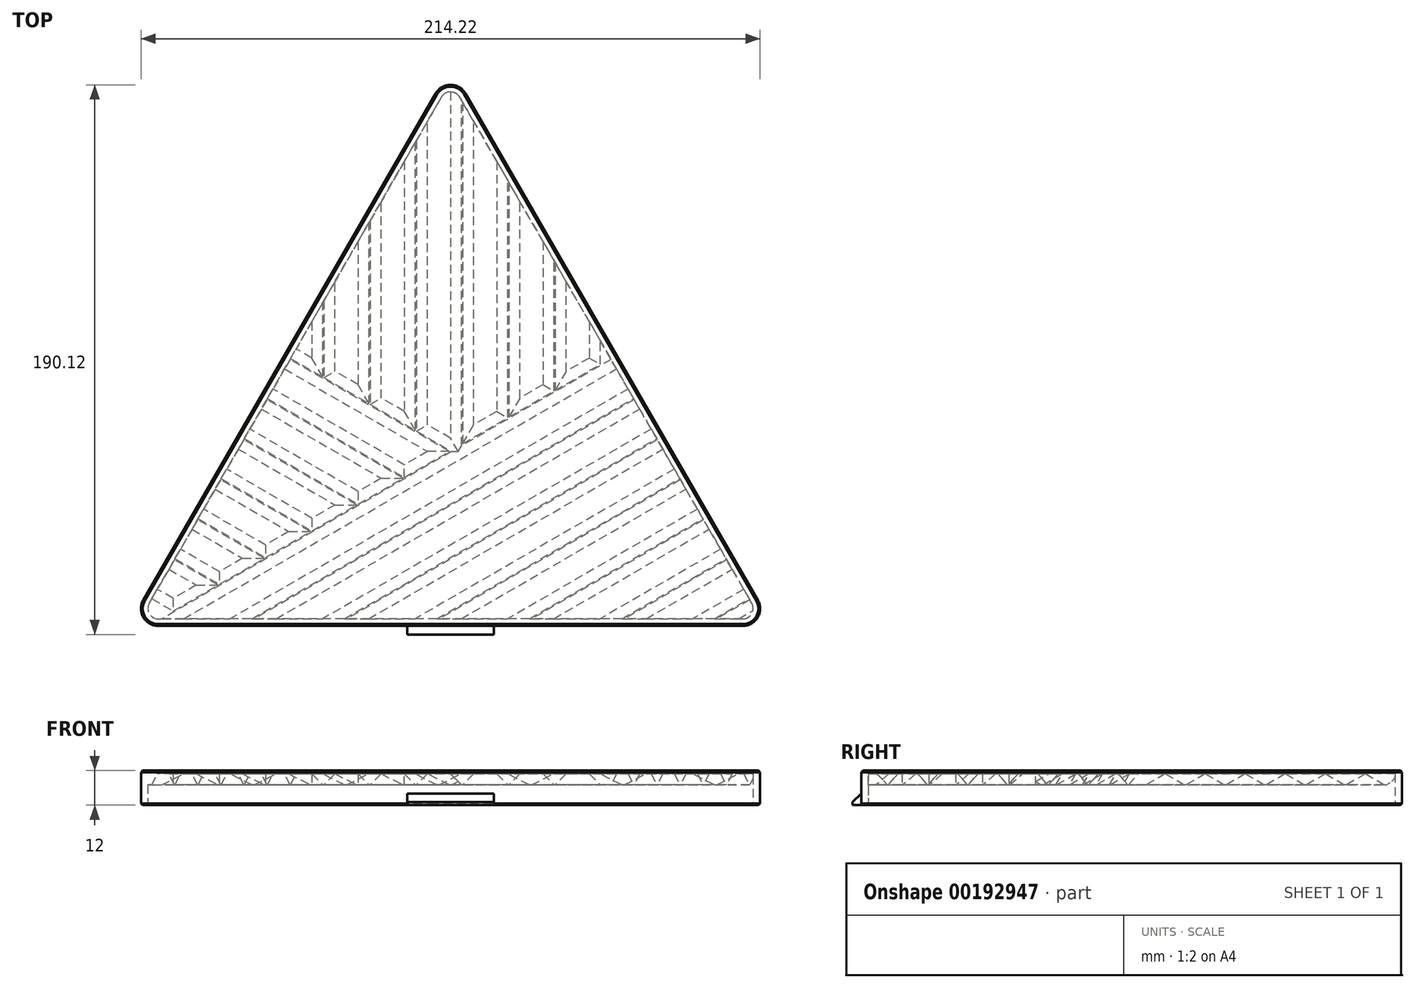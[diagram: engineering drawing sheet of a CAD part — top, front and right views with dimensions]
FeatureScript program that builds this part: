
annotation { "Feature Type Name" : "Feature", "Feature Type Description" : "" }
export const myFeature = defineFeature(function(context is Context, id is Id, definition is map)
    precondition{}
    {
        {
            var Q0;
            Q0=qCreatedBy(makeId("Top.planeOp"),FACE);
            var sketch = newSketch(context, id + "F0", { "sketchPlane" : qUnion([Q0])});
            skLineSegment(sketch, "E0", {"start": v(-5.2, -9) * mm, "end": v(-106.3, -184.12) * mm});
            skLineSegment(sketch, "E1", {"start": v(-101.1, -193.12) * mm, "end": v(101.1, -193.12) * mm});
            skLineSegment(sketch, "E2", {"start": v(106.3, -184.12) * mm, "end": v(5.2, -9) * mm});
            skPoint(sketch, "E3.visualSharp", {"position": v(-111.5, -193.12) * mm});
            skArc(sketch, "E3.filletArc", {"start": v(-106.3, -184.12) * mm, "mid": v(-106.3, -190.12) * mm, "end": v(-101.1, -193.12) * mm});
            skPoint(sketch, "E4.visualSharp", {"position": v(111.5, -193.12) * mm});
            skArc(sketch, "E4.filletArc", {"start": v(101.1, -193.12) * mm, "mid": v(106.3, -190.12) * mm, "end": v(106.3, -184.12) * mm});
            skPoint(sketch, "E5.visualSharp", {"position": v(0, 0) * mm});
            skArc(sketch, "E5.filletArc", {"start": v(5.2, -9) * mm, "mid": v(0, -6) * mm, "end": v(-5.2, -9) * mm});
            skSolve(sketch);
        }
        {
            var Q0;
            Q0=qSketchRegion(id+"F0",true);
            extrude(context, id + "F1", {"entities" : qUnion([Q0]), "depth" : 12 * mm});
        }
        {
            var Q0;
            Q0=makeQuery(id+"F1.opExtrude","CAP_FACE",FACE,{"disambiguationData":[OSD([sQuery(id+"F0.wireOp",EDGE,"E0"),sQuery(id+"F0.wireOp",EDGE,"E1"),sQuery(id+"F0.wireOp",EDGE,"E2"),sQuery(id+"F0.wireOp",EDGE,"E3.filletArc"),sQuery(id+"F0.wireOp",EDGE,"E4.filletArc"),sQuery(id+"F0.wireOp",EDGE,"E5.filletArc")])],"isStart":true});
            shell(context, id + "F2", {"entities" : qUnion([Q0]), "thickness" : 1 * mm});
        }
        {
            var Q0;
            Q0=makeQuery(id+"F1.opExtrude","CAP_FACE",FACE,{"disambiguationData":[OSD([sQuery(id+"F0.wireOp",EDGE,"E0"),sQuery(id+"F0.wireOp",EDGE,"E1"),sQuery(id+"F0.wireOp",EDGE,"E2"),sQuery(id+"F0.wireOp",EDGE,"E3.filletArc"),sQuery(id+"F0.wireOp",EDGE,"E4.filletArc"),sQuery(id+"F0.wireOp",EDGE,"E5.filletArc")])],"isStart":false});
            var sketch = newSketch(context, id + "F3", { "sketchPlane" : qUnion([Q0])});
            skArc(sketch, "E6.0.0", {"start": v(5.2, -9) * mm, "mid": v(0, -6) * mm, "end": v(-5.2, -9) * mm});
            skLineSegment(sketch, "E6.0.1", {"start": v(-5.2, -9) * mm, "end": v(-106.3, -184.12) * mm});
            skArc(sketch, "E6.0.2", {"start": v(-105.74, -183.31) * mm, "mid": v(-106.53, -189.68) * mm, "end": v(-101.1, -193.12) * mm});
            skLineSegment(sketch, "E6.0.3", {"start": v(-101.1, -193.12) * mm, "end": v(101.1, -193.12) * mm});
            skArc(sketch, "E6.0.4", {"start": v(101.1, -193.12) * mm, "mid": v(106.3, -190.12) * mm, "end": v(106.3, -184.12) * mm});
            skLineSegment(sketch, "E6.0.5", {"start": v(106.3, -184.12) * mm, "end": v(5.2, -9) * mm});
            skLineSegment(sketch, "E7", {"start": v(55.5, -96.13) * mm, "end": v(-105.8, -189.26) * mm});
            skLineSegment(sketch, "E8", {"start": v(-55.5, -96.13) * mm, "end": v(0, -128.17) * mm});
            skLineSegment(sketch, "E9", {"start": v(0, -6) * mm, "end": v(0, -128.17) * mm});
            skLineSegment(sketch, "E10.1.0.0", {"start": v(8, -6) * mm, "end": v(8, -123.55) * mm});
            skLineSegment(sketch, "E10.2.0.0", {"start": v(16, -6) * mm, "end": v(16, -118.93) * mm});
            skLineSegment(sketch, "E10.3.0.0", {"start": v(24, -6) * mm, "end": v(24, -114.32) * mm});
            skLineSegment(sketch, "E10.4.0.0", {"start": v(32, -6) * mm, "end": v(32, -109.7) * mm});
            skLineSegment(sketch, "E10.5.0.0", {"start": v(40, -6) * mm, "end": v(40, -105.08) * mm});
            skLineSegment(sketch, "E10.6.0.0", {"start": v(48, -6) * mm, "end": v(48, -100.46) * mm});
            skLineSegment(sketch, "E10.7.0.0", {"start": v(56, -6) * mm, "end": v(56, -97) * mm});
            skLineSegment(sketch, "E10.direction1", {"start": v(0, -128.17) * mm, "end": v(8, -128.17) * mm, "construction": true});
            skLineSegment(sketch, "E11.1.0.0", {"start": v(-8, -6) * mm, "end": v(-8, -123.55) * mm});
            skLineSegment(sketch, "E11.2.0.0", {"start": v(-16, -6) * mm, "end": v(-16, -118.93) * mm});
            skLineSegment(sketch, "E11.3.0.0", {"start": v(-24, -6) * mm, "end": v(-24, -114.32) * mm});
            skLineSegment(sketch, "E11.4.0.0", {"start": v(-32, -6) * mm, "end": v(-32, -109.7) * mm});
            skLineSegment(sketch, "E11.5.0.0", {"start": v(-40, -6) * mm, "end": v(-40, -105.08) * mm});
            skLineSegment(sketch, "E11.6.0.0", {"start": v(-48, -6) * mm, "end": v(-48, -100.46) * mm});
            skLineSegment(sketch, "E11.7.0.0", {"start": v(-56, -6) * mm, "end": v(-56, -97) * mm});
            skLineSegment(sketch, "E11.direction1", {"start": v(0, -128.17) * mm, "end": v(-8, -128.17) * mm, "construction": true});
            skPoint(sketch, "E12.orphan", {"position": v(-56, -128.17) * mm});
            skPoint(sketch, "E13.orphan", {"position": v(-48, -128.17) * mm});
            skPoint(sketch, "E14.orphan", {"position": v(-40, -128.17) * mm});
            skPoint(sketch, "E15.orphan", {"position": v(-32, -128.17) * mm});
            skPoint(sketch, "E16.orphan", {"position": v(-24, -128.17) * mm});
            skPoint(sketch, "E17.orphan", {"position": v(-16, -128.17) * mm});
            skPoint(sketch, "E18.orphan", {"position": v(56, -128.17) * mm});
            skPoint(sketch, "E19.orphan", {"position": v(48, -128.17) * mm});
            skPoint(sketch, "E20.orphan", {"position": v(40, -128.17) * mm});
            skPoint(sketch, "E21.orphan", {"position": v(32, -128.17) * mm});
            skPoint(sketch, "E22.orphan", {"position": v(24, -128.17) * mm});
            skPoint(sketch, "E23.orphan", {"position": v(16, -128.17) * mm});
            skLineSegment(sketch, "E24.1.0.0", {"start": v(-59.49, -103.06) * mm, "end": v(-8, -132.8) * mm});
            skLineSegment(sketch, "E24.2.0.0", {"start": v(-63.48, -110) * mm, "end": v(-16, -137.4) * mm});
            skLineSegment(sketch, "E24.3.0.0", {"start": v(-67.46, -116.93) * mm, "end": v(-24, -142.03) * mm});
            skLineSegment(sketch, "E24.4.0.0", {"start": v(-71.45, -123.87) * mm, "end": v(-32, -146.65) * mm});
            skLineSegment(sketch, "E24.5.0.0", {"start": v(-75.44, -130.8) * mm, "end": v(-40, -151.27) * mm});
            skLineSegment(sketch, "E24.6.0.0", {"start": v(-79.43, -137.74) * mm, "end": v(-48, -155.88) * mm});
            skLineSegment(sketch, "E24.7.0.0", {"start": v(-83.41, -144.68) * mm, "end": v(-56, -160.5) * mm});
            skLineSegment(sketch, "E24.8.0.0", {"start": v(-87.4, -151.61) * mm, "end": v(-64, -165.12) * mm});
            skLineSegment(sketch, "E24.9.0.0", {"start": v(-91.39, -158.55) * mm, "end": v(-72, -169.74) * mm});
            skLineSegment(sketch, "E24.10.0.0", {"start": v(-95.38, -165.48) * mm, "end": v(-80, -174.36) * mm});
            skLineSegment(sketch, "E24.11.0.0", {"start": v(-99.36, -172.42) * mm, "end": v(-88, -178.98) * mm});
            skLineSegment(sketch, "E24.12.0.0", {"start": v(-103.35, -179.35) * mm, "end": v(-96, -183.6) * mm});
            skLineSegment(sketch, "E24.13.0.0", {"start": v(-107.34, -186.29) * mm, "end": v(-104, -188.22) * mm});
            skLineSegment(sketch, "E24.direction1", {"start": v(-55.5, -96.13) * mm, "end": v(-59.49, -103.06) * mm, "construction": true});
            skLineSegment(sketch, "E25.1.0.0", {"start": v(59.5, -103.05) * mm, "end": v(-101.8, -196.18) * mm});
            skLineSegment(sketch, "E25.2.0.0", {"start": v(63.51, -109.98) * mm, "end": v(-97.8, -203.1) * mm});
            skLineSegment(sketch, "E25.3.0.0", {"start": v(67.52, -116.9) * mm, "end": v(-93.79, -210.03) * mm});
            skLineSegment(sketch, "E25.4.0.0", {"start": v(71.52, -123.83) * mm, "end": v(-89.78, -216.96) * mm});
            skLineSegment(sketch, "E25.5.0.0", {"start": v(75.53, -130.75) * mm, "end": v(-85.78, -223.88) * mm});
            skLineSegment(sketch, "E25.6.0.0", {"start": v(79.53, -137.68) * mm, "end": v(-81.77, -230.8) * mm});
            skLineSegment(sketch, "E25.7.0.0", {"start": v(83.54, -144.6) * mm, "end": v(-77.77, -237.73) * mm});
            skLineSegment(sketch, "E25.8.0.0", {"start": v(87.54, -151.53) * mm, "end": v(-73.76, -244.66) * mm});
            skLineSegment(sketch, "E25.9.0.0", {"start": v(91.55, -158.46) * mm, "end": v(-69.76, -251.58) * mm});
            skLineSegment(sketch, "E25.10.0.0", {"start": v(95.55, -165.38) * mm, "end": v(-65.75, -258.5) * mm});
            skLineSegment(sketch, "E25.11.0.0", {"start": v(99.56, -172.3) * mm, "end": v(-61.75, -265.43) * mm});
            skLineSegment(sketch, "E25.12.0.0", {"start": v(103.56, -179.23) * mm, "end": v(-57.74, -272.36) * mm});
            skLineSegment(sketch, "E25.13.0.0", {"start": v(107.57, -186.16) * mm, "end": v(-53.73, -279.28) * mm});
            skLineSegment(sketch, "E25.direction1", {"start": v(-105.8, -189.26) * mm, "end": v(-101.8, -196.18) * mm, "construction": true});
            skLineSegment(sketch, "E26.trimOffspring", {"start": v(8, -132.8) * mm, "end": v(16, -137.4) * mm});
            skLineSegment(sketch, "E27.trimOffspring", {"start": v(0, -137.4) * mm, "end": v(8, -142.03) * mm});
            skLineSegment(sketch, "E28.trimOffspring", {"start": v(-8, -142.03) * mm, "end": v(0, -146.65) * mm});
            skLineSegment(sketch, "E29.trimOffspring", {"start": v(-16, -146.65) * mm, "end": v(-8, -151.27) * mm});
            skLineSegment(sketch, "E30.trimOffspring", {"start": v(-24, -151.27) * mm, "end": v(-16, -155.88) * mm});
            skLineSegment(sketch, "E31.trimOffspring", {"start": v(-32, -155.88) * mm, "end": v(-24, -160.5) * mm});
            skLineSegment(sketch, "E32.trimOffspring", {"start": v(-40, -160.5) * mm, "end": v(-32, -165.12) * mm});
            skLineSegment(sketch, "E33.trimOffspring", {"start": v(-48, -165.12) * mm, "end": v(-40, -169.74) * mm});
            skLineSegment(sketch, "E34.trimOffspring", {"start": v(-56, -169.74) * mm, "end": v(-48, -174.36) * mm});
            skLineSegment(sketch, "E35.trimOffspring", {"start": v(-64, -174.36) * mm, "end": v(64.72, -248.68) * mm});
            skLineSegment(sketch, "E36.trimOffspring", {"start": v(-72, -178.98) * mm, "end": v(60.73, -255.61) * mm});
            skLineSegment(sketch, "E37.trimOffspring", {"start": v(-80, -183.6) * mm, "end": v(56.74, -262.55) * mm});
            skLineSegment(sketch, "E38.trimOffspring", {"start": v(-88, -188.22) * mm, "end": v(52.76, -269.48) * mm});
            skLineSegment(sketch, "E39.trimOffspring", {"start": v(-97, -192.26) * mm, "end": v(48.77, -276.42) * mm});
            skLineSegment(sketch, "E40.trimOffspring", {"start": v(24, -142.03) * mm, "end": v(100.6, -186.26) * mm});
            skLineSegment(sketch, "E41.trimOffspring", {"start": v(16, -146.65) * mm, "end": v(96.62, -193.2) * mm});
            skLineSegment(sketch, "E42.trimOffspring", {"start": v(8, -151.27) * mm, "end": v(92.63, -200.13) * mm});
            skLineSegment(sketch, "E43.trimOffspring", {"start": v(0, -155.88) * mm, "end": v(88.65, -207.06) * mm});
            skLineSegment(sketch, "E44.trimOffspring", {"start": v(-8, -160.5) * mm, "end": v(84.66, -214) * mm});
            skLineSegment(sketch, "E45.trimOffspring", {"start": v(-16, -165.12) * mm, "end": v(80.67, -220.93) * mm});
            skLineSegment(sketch, "E46.trimOffspring", {"start": v(-24, -169.74) * mm, "end": v(76.68, -227.87) * mm});
            skLineSegment(sketch, "E47.trimOffspring", {"start": v(-32, -174.36) * mm, "end": v(72.7, -234.8) * mm});
            skLineSegment(sketch, "E48.trimOffspring", {"start": v(-40, -178.98) * mm, "end": v(68.7, -241.74) * mm});
            skSolve(sketch);
        }
        {
            var Q0;
            {var subQ0=sQuery(id+"F3.wireOp",EDGE,"E11.5.0.0");var subQ1=sQuery(id+"F3.wireOp",EDGE,"E6.0.1");var subQ2=makeQuery(id+"F3.imprint","INTERSECT",VERTEX,{"derivedFrom":[subQ1,subQ0]});Q0=makeQuery(id+"F3.imprint","IMPRINT",FACE,{"disambiguationData":[TD([[makeQuery(id+"F3.imprint","IMPRINT",EDGE,{"disambiguationData":[TD([[subQ2,-1.0]])],"derivedFrom":subQ1}),1.0]])]});}
            var Q1;
            {var subQ0=sQuery(id+"F3.wireOp",EDGE,"E11.3.0.0");var subQ1=sQuery(id+"F3.wireOp",EDGE,"E6.0.1");var subQ2=makeQuery(id+"F3.imprint","INTERSECT",VERTEX,{"derivedFrom":[subQ1,subQ0]});Q1=makeQuery(id+"F3.imprint","IMPRINT",FACE,{"disambiguationData":[TD([[makeQuery(id+"F3.imprint","IMPRINT",EDGE,{"disambiguationData":[TD([[subQ2,-1.0]])],"derivedFrom":subQ1}),1.0]])]});}
            var Q2;
            {var subQ0=sQuery(id+"F3.wireOp",EDGE,"E11.1.0.0");var subQ1=sQuery(id+"F3.wireOp",EDGE,"E6.0.1");var subQ2=makeQuery(id+"F3.imprint","INTERSECT",VERTEX,{"derivedFrom":[subQ1,subQ0]});Q2=makeQuery(id+"F3.imprint","IMPRINT",FACE,{"disambiguationData":[TD([[makeQuery(id+"F3.imprint","IMPRINT",EDGE,{"disambiguationData":[TD([[subQ2,-1.0]])],"derivedFrom":subQ1}),1.0]])]});}
            var Q3;
            {var subQ0=sQuery(id+"F3.wireOp",EDGE,"E9");Q3=makeQuery(id+"F3.imprint","IMPRINT",FACE,{"disambiguationData":[TD([[makeQuery(id+"F3.imprint","IMPRINT",EDGE,{"derivedFrom":subQ0}),1.0]])]});}
            var Q4;
            {var subQ0=sQuery(id+"F3.wireOp",EDGE,"E10.3.0.0");var subQ1=sQuery(id+"F3.wireOp",EDGE,"E6.0.5");var subQ2=makeQuery(id+"F3.imprint","INTERSECT",VERTEX,{"derivedFrom":[subQ1,subQ0]});Q4=makeQuery(id+"F3.imprint","IMPRINT",FACE,{"disambiguationData":[TD([[makeQuery(id+"F3.imprint","IMPRINT",EDGE,{"disambiguationData":[TD([[subQ2,-1.0]])],"derivedFrom":subQ1}),1.0]])]});}
            var Q5;
            {var subQ0=sQuery(id+"F3.wireOp",EDGE,"E10.5.0.0");var subQ1=sQuery(id+"F3.wireOp",EDGE,"E6.0.5");var subQ2=makeQuery(id+"F3.imprint","INTERSECT",VERTEX,{"derivedFrom":[subQ1,subQ0]});Q5=makeQuery(id+"F3.imprint","IMPRINT",FACE,{"disambiguationData":[TD([[makeQuery(id+"F3.imprint","IMPRINT",EDGE,{"disambiguationData":[TD([[subQ2,-1.0]])],"derivedFrom":subQ1}),1.0]])]});}
            var Q6;
            {var subQ0=sQuery(id+"F3.wireOp",EDGE,"E7");var subQ1=sQuery(id+"F3.wireOp",EDGE,"E6.0.5");var subQ2=makeQuery(id+"F3.imprint","INTERSECT",VERTEX,{"derivedFrom":[subQ1,subQ0]});Q6=makeQuery(id+"F3.imprint","IMPRINT",FACE,{"disambiguationData":[TD([[makeQuery(id+"F3.imprint","IMPRINT",EDGE,{"disambiguationData":[TD([[subQ2,-1.0]])],"derivedFrom":subQ1}),1.0]])]});}
            var Q7;
            {var subQ0=sQuery(id+"F3.wireOp",EDGE,"E7");var subQ17=makeQuery(id+"F3.imprint","IMPRINT",VERTEX,{"disambiguationData":[OD(0.0)],"derivedFrom":subQ0});Q7=makeQuery(id+"F3.imprint","IMPRINT",FACE,{"disambiguationData":[TD([[makeQuery(id+"F3.imprint","IMPRINT",EDGE,{"disambiguationData":[TD([[subQ17,-1.0]])],"derivedFrom":subQ0}),1.0]])]});}
            var Q8;
            {var subQ5=sQuery(id+"F3.wireOp",EDGE,"E25.3.0.0");var subQ17=sQuery(id+"F3.wireOp",EDGE,"E6.0.5");var subQ20=makeQuery(id+"F3.imprint","INTERSECT",VERTEX,{"derivedFrom":[subQ17,subQ5]});Q8=makeQuery(id+"F3.imprint","IMPRINT",FACE,{"disambiguationData":[TD([[makeQuery(id+"F3.imprint","IMPRINT",EDGE,{"disambiguationData":[TD([[subQ20,-1.0]])],"derivedFrom":subQ17}),1.0]])]});}
            var Q9;
            {var subQ0=sQuery(id+"F3.wireOp",EDGE,"E35.trimOffspring");var subQ1=sQuery(id+"F3.wireOp",EDGE,"E25.2.0.0");var subQ2=makeQuery(id+"F3.imprint","INTERSECT",VERTEX,{"derivedFrom":[subQ1,subQ0]});Q9=makeQuery(id+"F3.imprint","IMPRINT",FACE,{"disambiguationData":[TD([[makeQuery(id+"F3.imprint","IMPRINT",EDGE,{"disambiguationData":[TD([[subQ2,-1.0]])],"derivedFrom":subQ1}),1.0]])]});}
            var Q10;
            {var subQ0=sQuery(id+"F3.wireOp",EDGE,"E25.2.0.0");var subQ1=sQuery(id+"F3.wireOp",EDGE,"E6.0.3");var subQ2=makeQuery(id+"F3.imprint","INTERSECT",VERTEX,{"derivedFrom":[subQ1,subQ0]});Q10=makeQuery(id+"F3.imprint","IMPRINT",FACE,{"disambiguationData":[TD([[makeQuery(id+"F3.imprint","IMPRINT",EDGE,{"disambiguationData":[TD([[subQ2,-1.0]])],"derivedFrom":subQ1}),1.0]])]});}
            var Q11;
            {var subQ0=sQuery(id+"F3.wireOp",EDGE,"E25.5.0.0");var subQ1=sQuery(id+"F3.wireOp",EDGE,"E6.0.5");var subQ2=makeQuery(id+"F3.imprint","INTERSECT",VERTEX,{"derivedFrom":[subQ1,subQ0]});Q11=makeQuery(id+"F3.imprint","IMPRINT",FACE,{"disambiguationData":[TD([[makeQuery(id+"F3.imprint","IMPRINT",EDGE,{"disambiguationData":[TD([[subQ2,-1.0]])],"derivedFrom":subQ1}),1.0]])]});}
            var Q12;
            {var subQ0=sQuery(id+"F3.wireOp",EDGE,"E40.trimOffspring");var subQ1=sQuery(id+"F3.wireOp",EDGE,"E25.4.0.0");var subQ2=makeQuery(id+"F3.imprint","INTERSECT",VERTEX,{"derivedFrom":[subQ1,subQ0]});Q12=makeQuery(id+"F3.imprint","IMPRINT",FACE,{"disambiguationData":[TD([[makeQuery(id+"F3.imprint","IMPRINT",EDGE,{"disambiguationData":[TD([[subQ2,-1.0]])],"derivedFrom":subQ1}),1.0]])]});}
            var Q13;
            {var subQ0=sQuery(id+"F3.wireOp",EDGE,"E41.trimOffspring");var subQ1=sQuery(id+"F3.wireOp",EDGE,"E25.4.0.0");var subQ2=makeQuery(id+"F3.imprint","INTERSECT",VERTEX,{"derivedFrom":[subQ1,subQ0]});Q13=makeQuery(id+"F3.imprint","IMPRINT",FACE,{"disambiguationData":[TD([[makeQuery(id+"F3.imprint","IMPRINT",EDGE,{"disambiguationData":[TD([[subQ2,-1.0]])],"derivedFrom":subQ1}),1.0]])]});}
            var Q14;
            {var subQ0=sQuery(id+"F3.wireOp",EDGE,"E42.trimOffspring");var subQ1=sQuery(id+"F3.wireOp",EDGE,"E25.4.0.0");var subQ2=makeQuery(id+"F3.imprint","INTERSECT",VERTEX,{"derivedFrom":[subQ1,subQ0]});Q14=makeQuery(id+"F3.imprint","IMPRINT",FACE,{"disambiguationData":[TD([[makeQuery(id+"F3.imprint","IMPRINT",EDGE,{"disambiguationData":[TD([[subQ2,-1.0]])],"derivedFrom":subQ1}),1.0]])]});}
            var Q15;
            {var subQ0=sQuery(id+"F3.wireOp",EDGE,"E43.trimOffspring");var subQ1=sQuery(id+"F3.wireOp",EDGE,"E25.4.0.0");var subQ2=makeQuery(id+"F3.imprint","INTERSECT",VERTEX,{"derivedFrom":[subQ1,subQ0]});Q15=makeQuery(id+"F3.imprint","IMPRINT",FACE,{"disambiguationData":[TD([[makeQuery(id+"F3.imprint","IMPRINT",EDGE,{"disambiguationData":[TD([[subQ2,-1.0]])],"derivedFrom":subQ1}),1.0]])]});}
            var Q16;
            {var subQ0=sQuery(id+"F3.wireOp",EDGE,"E44.trimOffspring");var subQ1=sQuery(id+"F3.wireOp",EDGE,"E25.4.0.0");var subQ2=makeQuery(id+"F3.imprint","INTERSECT",VERTEX,{"derivedFrom":[subQ1,subQ0]});Q16=makeQuery(id+"F3.imprint","IMPRINT",FACE,{"disambiguationData":[TD([[makeQuery(id+"F3.imprint","IMPRINT",EDGE,{"disambiguationData":[TD([[subQ2,-1.0]])],"derivedFrom":subQ1}),1.0]])]});}
            var Q17;
            {var subQ0=sQuery(id+"F3.wireOp",EDGE,"E45.trimOffspring");var subQ1=sQuery(id+"F3.wireOp",EDGE,"E25.4.0.0");var subQ2=makeQuery(id+"F3.imprint","INTERSECT",VERTEX,{"derivedFrom":[subQ1,subQ0]});Q17=makeQuery(id+"F3.imprint","IMPRINT",FACE,{"disambiguationData":[TD([[makeQuery(id+"F3.imprint","IMPRINT",EDGE,{"disambiguationData":[TD([[subQ2,-1.0]])],"derivedFrom":subQ1}),1.0]])]});}
            var Q18;
            {var subQ0=sQuery(id+"F3.wireOp",EDGE,"E46.trimOffspring");var subQ1=sQuery(id+"F3.wireOp",EDGE,"E25.4.0.0");var subQ2=makeQuery(id+"F3.imprint","INTERSECT",VERTEX,{"derivedFrom":[subQ1,subQ0]});Q18=makeQuery(id+"F3.imprint","IMPRINT",FACE,{"disambiguationData":[TD([[makeQuery(id+"F3.imprint","IMPRINT",EDGE,{"disambiguationData":[TD([[subQ2,-1.0]])],"derivedFrom":subQ1}),1.0]])]});}
            var Q19;
            {var subQ0=sQuery(id+"F3.wireOp",EDGE,"E47.trimOffspring");var subQ1=sQuery(id+"F3.wireOp",EDGE,"E25.4.0.0");var subQ2=makeQuery(id+"F3.imprint","INTERSECT",VERTEX,{"derivedFrom":[subQ1,subQ0]});Q19=makeQuery(id+"F3.imprint","IMPRINT",FACE,{"disambiguationData":[TD([[makeQuery(id+"F3.imprint","IMPRINT",EDGE,{"disambiguationData":[TD([[subQ2,-1.0]])],"derivedFrom":subQ1}),1.0]])]});}
            var Q20;
            {var subQ0=sQuery(id+"F3.wireOp",EDGE,"E25.4.0.0");var subQ1=sQuery(id+"F3.wireOp",EDGE,"E6.0.3");var subQ2=makeQuery(id+"F3.imprint","INTERSECT",VERTEX,{"derivedFrom":[subQ1,subQ0]});Q20=makeQuery(id+"F3.imprint","IMPRINT",FACE,{"disambiguationData":[TD([[makeQuery(id+"F3.imprint","IMPRINT",EDGE,{"disambiguationData":[TD([[subQ2,-1.0]])],"derivedFrom":subQ1}),1.0]])]});}
            var Q21;
            {var subQ0=sQuery(id+"F3.wireOp",EDGE,"E25.6.0.0");var subQ1=sQuery(id+"F3.wireOp",EDGE,"E6.0.3");var subQ2=makeQuery(id+"F3.imprint","INTERSECT",VERTEX,{"derivedFrom":[subQ1,subQ0]});Q21=makeQuery(id+"F3.imprint","IMPRINT",FACE,{"disambiguationData":[TD([[makeQuery(id+"F3.imprint","IMPRINT",EDGE,{"disambiguationData":[TD([[subQ2,-1.0]])],"derivedFrom":subQ1}),1.0]])]});}
            var Q22;
            {var subQ0=sQuery(id+"F3.wireOp",EDGE,"E45.trimOffspring");var subQ1=sQuery(id+"F3.wireOp",EDGE,"E25.6.0.0");var subQ2=makeQuery(id+"F3.imprint","INTERSECT",VERTEX,{"derivedFrom":[subQ1,subQ0]});Q22=makeQuery(id+"F3.imprint","IMPRINT",FACE,{"disambiguationData":[TD([[makeQuery(id+"F3.imprint","IMPRINT",EDGE,{"disambiguationData":[TD([[subQ2,-1.0]])],"derivedFrom":subQ1}),1.0]])]});}
            var Q23;
            {var subQ0=sQuery(id+"F3.wireOp",EDGE,"E44.trimOffspring");var subQ1=sQuery(id+"F3.wireOp",EDGE,"E25.6.0.0");var subQ2=makeQuery(id+"F3.imprint","INTERSECT",VERTEX,{"derivedFrom":[subQ1,subQ0]});Q23=makeQuery(id+"F3.imprint","IMPRINT",FACE,{"disambiguationData":[TD([[makeQuery(id+"F3.imprint","IMPRINT",EDGE,{"disambiguationData":[TD([[subQ2,-1.0]])],"derivedFrom":subQ1}),1.0]])]});}
            var Q24;
            {var subQ0=sQuery(id+"F3.wireOp",EDGE,"E43.trimOffspring");var subQ1=sQuery(id+"F3.wireOp",EDGE,"E25.6.0.0");var subQ2=makeQuery(id+"F3.imprint","INTERSECT",VERTEX,{"derivedFrom":[subQ1,subQ0]});Q24=makeQuery(id+"F3.imprint","IMPRINT",FACE,{"disambiguationData":[TD([[makeQuery(id+"F3.imprint","IMPRINT",EDGE,{"disambiguationData":[TD([[subQ2,-1.0]])],"derivedFrom":subQ1}),1.0]])]});}
            var Q25;
            {var subQ0=sQuery(id+"F3.wireOp",EDGE,"E42.trimOffspring");var subQ1=sQuery(id+"F3.wireOp",EDGE,"E25.6.0.0");var subQ2=makeQuery(id+"F3.imprint","INTERSECT",VERTEX,{"derivedFrom":[subQ1,subQ0]});Q25=makeQuery(id+"F3.imprint","IMPRINT",FACE,{"disambiguationData":[TD([[makeQuery(id+"F3.imprint","IMPRINT",EDGE,{"disambiguationData":[TD([[subQ2,-1.0]])],"derivedFrom":subQ1}),1.0]])]});}
            var Q26;
            {var subQ0=sQuery(id+"F3.wireOp",EDGE,"E41.trimOffspring");var subQ1=sQuery(id+"F3.wireOp",EDGE,"E25.6.0.0");var subQ2=makeQuery(id+"F3.imprint","INTERSECT",VERTEX,{"derivedFrom":[subQ1,subQ0]});Q26=makeQuery(id+"F3.imprint","IMPRINT",FACE,{"disambiguationData":[TD([[makeQuery(id+"F3.imprint","IMPRINT",EDGE,{"disambiguationData":[TD([[subQ2,-1.0]])],"derivedFrom":subQ1}),1.0]])]});}
            var Q27;
            {var subQ0=sQuery(id+"F3.wireOp",EDGE,"E40.trimOffspring");var subQ1=sQuery(id+"F3.wireOp",EDGE,"E25.6.0.0");var subQ2=makeQuery(id+"F3.imprint","INTERSECT",VERTEX,{"derivedFrom":[subQ1,subQ0]});Q27=makeQuery(id+"F3.imprint","IMPRINT",FACE,{"disambiguationData":[TD([[makeQuery(id+"F3.imprint","IMPRINT",EDGE,{"disambiguationData":[TD([[subQ2,-1.0]])],"derivedFrom":subQ1}),1.0]])]});}
            var Q28;
            {var subQ0=sQuery(id+"F3.wireOp",EDGE,"E25.7.0.0");var subQ1=sQuery(id+"F3.wireOp",EDGE,"E6.0.5");var subQ2=makeQuery(id+"F3.imprint","INTERSECT",VERTEX,{"derivedFrom":[subQ1,subQ0]});Q28=makeQuery(id+"F3.imprint","IMPRINT",FACE,{"disambiguationData":[TD([[makeQuery(id+"F3.imprint","IMPRINT",EDGE,{"disambiguationData":[TD([[subQ2,-1.0]])],"derivedFrom":subQ1}),1.0]])]});}
            var Q29;
            {var subQ0=sQuery(id+"F3.wireOp",EDGE,"E25.9.0.0");var subQ1=sQuery(id+"F3.wireOp",EDGE,"E6.0.5");var subQ2=makeQuery(id+"F3.imprint","INTERSECT",VERTEX,{"derivedFrom":[subQ1,subQ0]});Q29=makeQuery(id+"F3.imprint","IMPRINT",FACE,{"disambiguationData":[TD([[makeQuery(id+"F3.imprint","IMPRINT",EDGE,{"disambiguationData":[TD([[subQ2,-1.0]])],"derivedFrom":subQ1}),1.0]])]});}
            var Q30;
            {var subQ0=sQuery(id+"F3.wireOp",EDGE,"E40.trimOffspring");var subQ1=sQuery(id+"F3.wireOp",EDGE,"E25.8.0.0");var subQ2=makeQuery(id+"F3.imprint","INTERSECT",VERTEX,{"derivedFrom":[subQ1,subQ0]});Q30=makeQuery(id+"F3.imprint","IMPRINT",FACE,{"disambiguationData":[TD([[makeQuery(id+"F3.imprint","IMPRINT",EDGE,{"disambiguationData":[TD([[subQ2,-1.0]])],"derivedFrom":subQ1}),1.0]])]});}
            var Q31;
            {var subQ0=sQuery(id+"F3.wireOp",EDGE,"E41.trimOffspring");var subQ1=sQuery(id+"F3.wireOp",EDGE,"E25.8.0.0");var subQ2=makeQuery(id+"F3.imprint","INTERSECT",VERTEX,{"derivedFrom":[subQ1,subQ0]});Q31=makeQuery(id+"F3.imprint","IMPRINT",FACE,{"disambiguationData":[TD([[makeQuery(id+"F3.imprint","IMPRINT",EDGE,{"disambiguationData":[TD([[subQ2,-1.0]])],"derivedFrom":subQ1}),1.0]])]});}
            var Q32;
            {var subQ0=sQuery(id+"F3.wireOp",EDGE,"E43.trimOffspring");var subQ1=sQuery(id+"F3.wireOp",EDGE,"E25.8.0.0");var subQ2=makeQuery(id+"F3.imprint","INTERSECT",VERTEX,{"derivedFrom":[subQ1,subQ0]});Q32=makeQuery(id+"F3.imprint","IMPRINT",FACE,{"disambiguationData":[TD([[makeQuery(id+"F3.imprint","IMPRINT",EDGE,{"disambiguationData":[TD([[subQ2,-1.0]])],"derivedFrom":subQ1}),1.0]])]});}
            var Q33;
            {var subQ0=sQuery(id+"F3.wireOp",EDGE,"E25.8.0.0");var subQ1=sQuery(id+"F3.wireOp",EDGE,"E6.0.3");var subQ2=makeQuery(id+"F3.imprint","INTERSECT",VERTEX,{"derivedFrom":[subQ1,subQ0]});Q33=makeQuery(id+"F3.imprint","IMPRINT",FACE,{"disambiguationData":[TD([[makeQuery(id+"F3.imprint","IMPRINT",EDGE,{"disambiguationData":[TD([[subQ2,-1.0]])],"derivedFrom":subQ1}),1.0]])]});}
            var Q34;
            {var subQ0=sQuery(id+"F3.wireOp",EDGE,"E42.trimOffspring");var subQ1=sQuery(id+"F3.wireOp",EDGE,"E25.8.0.0");var subQ2=makeQuery(id+"F3.imprint","INTERSECT",VERTEX,{"derivedFrom":[subQ1,subQ0]});Q34=makeQuery(id+"F3.imprint","IMPRINT",FACE,{"disambiguationData":[TD([[makeQuery(id+"F3.imprint","IMPRINT",EDGE,{"disambiguationData":[TD([[subQ2,-1.0]])],"derivedFrom":subQ1}),1.0]])]});}
            var Q35;
            {var subQ0=sQuery(id+"F3.wireOp",EDGE,"E25.10.0.0");var subQ1=sQuery(id+"F3.wireOp",EDGE,"E6.0.3");var subQ2=makeQuery(id+"F3.imprint","INTERSECT",VERTEX,{"derivedFrom":[subQ1,subQ0]});Q35=makeQuery(id+"F3.imprint","IMPRINT",FACE,{"disambiguationData":[TD([[makeQuery(id+"F3.imprint","IMPRINT",EDGE,{"disambiguationData":[TD([[subQ2,-1.0]])],"derivedFrom":subQ1}),1.0]])]});}
            var Q36;
            {var subQ0=sQuery(id+"F3.wireOp",EDGE,"E41.trimOffspring");var subQ1=sQuery(id+"F3.wireOp",EDGE,"E25.10.0.0");var subQ2=makeQuery(id+"F3.imprint","INTERSECT",VERTEX,{"derivedFrom":[subQ1,subQ0]});Q36=makeQuery(id+"F3.imprint","IMPRINT",FACE,{"disambiguationData":[TD([[makeQuery(id+"F3.imprint","IMPRINT",EDGE,{"disambiguationData":[TD([[subQ2,-1.0]])],"derivedFrom":subQ1}),1.0]])]});}
            var Q37;
            {var subQ0=sQuery(id+"F3.wireOp",EDGE,"E40.trimOffspring");var subQ1=sQuery(id+"F3.wireOp",EDGE,"E25.10.0.0");var subQ2=makeQuery(id+"F3.imprint","INTERSECT",VERTEX,{"derivedFrom":[subQ1,subQ0]});Q37=makeQuery(id+"F3.imprint","IMPRINT",FACE,{"disambiguationData":[TD([[makeQuery(id+"F3.imprint","IMPRINT",EDGE,{"disambiguationData":[TD([[subQ2,-1.0]])],"derivedFrom":subQ1}),1.0]])]});}
            var Q38;
            {var subQ0=sQuery(id+"F3.wireOp",EDGE,"E25.11.0.0");var subQ1=sQuery(id+"F3.wireOp",EDGE,"E6.0.5");var subQ2=makeQuery(id+"F3.imprint","INTERSECT",VERTEX,{"derivedFrom":[subQ1,subQ0]});Q38=makeQuery(id+"F3.imprint","IMPRINT",FACE,{"disambiguationData":[TD([[makeQuery(id+"F3.imprint","IMPRINT",EDGE,{"disambiguationData":[TD([[subQ2,-1.0]])],"derivedFrom":subQ1}),1.0]])]});}
            var Q39;
            {var subQ0=sQuery(id+"F3.wireOp",EDGE,"E25.12.0.0");var subQ1=sQuery(id+"F3.wireOp",EDGE,"E6.0.3");var subQ2=makeQuery(id+"F3.imprint","INTERSECT",VERTEX,{"derivedFrom":[subQ1,subQ0]});Q39=makeQuery(id+"F3.imprint","IMPRINT",FACE,{"disambiguationData":[TD([[makeQuery(id+"F3.imprint","IMPRINT",EDGE,{"disambiguationData":[TD([[subQ2,-1.0]])],"derivedFrom":subQ1}),1.0]])]});}
            var Q40;
            {var subQ0=sQuery(id+"F3.wireOp",EDGE,"E42.trimOffspring");var subQ1=sQuery(id+"F3.wireOp",EDGE,"E25.10.0.0");var subQ2=makeQuery(id+"F3.imprint","INTERSECT",VERTEX,{"derivedFrom":[subQ1,subQ0]});Q40=makeQuery(id+"F3.imprint","IMPRINT",FACE,{"disambiguationData":[TD([[makeQuery(id+"F3.imprint","IMPRINT",EDGE,{"disambiguationData":[TD([[subQ2,-1.0]])],"derivedFrom":subQ1}),1.0]])]});}
            var Q41;
            {var subQ5=sQuery(id+"F3.wireOp",EDGE,"E6.0.3");var subQ7=sQuery(id+"F3.wireOp",EDGE,"E44.trimOffspring");var subQ9=makeQuery(id+"F3.imprint","INTERSECT",VERTEX,{"derivedFrom":[subQ5,subQ7]});Q41=makeQuery(id+"F3.imprint","IMPRINT",FACE,{"disambiguationData":[TD([[makeQuery(id+"F3.imprint","IMPRINT",EDGE,{"disambiguationData":[TD([[subQ9,-1.0]])],"derivedFrom":subQ5}),1.0]])]});}
            var Q42;
            {var subQ1=sQuery(id+"F3.wireOp",EDGE,"E6.0.3");var subQ7=sQuery(id+"F3.wireOp",EDGE,"E46.trimOffspring");var subQ9=makeQuery(id+"F3.imprint","INTERSECT",VERTEX,{"derivedFrom":[subQ1,subQ7]});Q42=makeQuery(id+"F3.imprint","IMPRINT",FACE,{"disambiguationData":[TD([[makeQuery(id+"F3.imprint","IMPRINT",EDGE,{"disambiguationData":[TD([[subQ9,-1.0]])],"derivedFrom":subQ1}),1.0]])]});}
            var Q43;
            {var subQ0=sQuery(id+"F3.wireOp",EDGE,"E44.trimOffspring");var subQ1=sQuery(id+"F3.wireOp",EDGE,"E25.8.0.0");var subQ2=makeQuery(id+"F3.imprint","INTERSECT",VERTEX,{"derivedFrom":[subQ1,subQ0]});Q43=makeQuery(id+"F3.imprint","IMPRINT",FACE,{"disambiguationData":[TD([[makeQuery(id+"F3.imprint","IMPRINT",EDGE,{"disambiguationData":[TD([[subQ2,-1.0]])],"derivedFrom":subQ1}),1.0]])]});}
            var Q44;
            {var subQ0=sQuery(id+"F3.wireOp",EDGE,"E46.trimOffspring");var subQ1=sQuery(id+"F3.wireOp",EDGE,"E25.6.0.0");var subQ2=makeQuery(id+"F3.imprint","INTERSECT",VERTEX,{"derivedFrom":[subQ1,subQ0]});Q44=makeQuery(id+"F3.imprint","IMPRINT",FACE,{"disambiguationData":[TD([[makeQuery(id+"F3.imprint","IMPRINT",EDGE,{"disambiguationData":[TD([[subQ2,-1.0]])],"derivedFrom":subQ1}),1.0]])]});}
            var Q45;
            {var subQ5=sQuery(id+"F3.wireOp",EDGE,"E6.0.3");var subQ7=sQuery(id+"F3.wireOp",EDGE,"E48.trimOffspring");var subQ9=makeQuery(id+"F3.imprint","INTERSECT",VERTEX,{"derivedFrom":[subQ5,subQ7]});Q45=makeQuery(id+"F3.imprint","IMPRINT",FACE,{"disambiguationData":[TD([[makeQuery(id+"F3.imprint","IMPRINT",EDGE,{"disambiguationData":[TD([[subQ9,-1.0]])],"derivedFrom":subQ5}),1.0]])]});}
            var Q46;
            {var subQ0=sQuery(id+"F3.wireOp",EDGE,"E48.trimOffspring");var subQ1=sQuery(id+"F3.wireOp",EDGE,"E25.4.0.0");var subQ2=makeQuery(id+"F3.imprint","INTERSECT",VERTEX,{"derivedFrom":[subQ1,subQ0]});Q46=makeQuery(id+"F3.imprint","IMPRINT",FACE,{"disambiguationData":[TD([[makeQuery(id+"F3.imprint","IMPRINT",EDGE,{"disambiguationData":[TD([[subQ2,-1.0]])],"derivedFrom":subQ1}),1.0]])]});}
            var Q47;
            {var subQ5=sQuery(id+"F3.wireOp",EDGE,"E6.0.3");var subQ7=sQuery(id+"F3.wireOp",EDGE,"E36.trimOffspring");var subQ9=makeQuery(id+"F3.imprint","INTERSECT",VERTEX,{"derivedFrom":[subQ5,subQ7]});Q47=makeQuery(id+"F3.imprint","IMPRINT",FACE,{"disambiguationData":[TD([[makeQuery(id+"F3.imprint","IMPRINT",EDGE,{"disambiguationData":[TD([[subQ9,-1.0]])],"derivedFrom":subQ5}),1.0]])]});}
            var Q48;
            {var subQ0=sQuery(id+"F3.wireOp",EDGE,"E36.trimOffspring");var subQ1=sQuery(id+"F3.wireOp",EDGE,"E25.2.0.0");var subQ2=makeQuery(id+"F3.imprint","INTERSECT",VERTEX,{"derivedFrom":[subQ1,subQ0]});Q48=makeQuery(id+"F3.imprint","IMPRINT",FACE,{"disambiguationData":[TD([[makeQuery(id+"F3.imprint","IMPRINT",EDGE,{"disambiguationData":[TD([[subQ2,-1.0]])],"derivedFrom":subQ1}),1.0]])]});}
            var Q49;
            {var subQ1=sQuery(id+"F3.wireOp",EDGE,"E6.0.3");var subQ7=sQuery(id+"F3.wireOp",EDGE,"E38.trimOffspring");var subQ9=makeQuery(id+"F3.imprint","INTERSECT",VERTEX,{"derivedFrom":[subQ1,subQ7]});Q49=makeQuery(id+"F3.imprint","IMPRINT",FACE,{"disambiguationData":[TD([[makeQuery(id+"F3.imprint","IMPRINT",EDGE,{"disambiguationData":[TD([[subQ9,-1.0]])],"derivedFrom":subQ1}),1.0]])]});}
            var Q50;
            {var subQ0=sQuery(id+"F3.wireOp",EDGE,"E25.13.0.0");var subQ1=sQuery(id+"F3.wireOp",EDGE,"E6.0.3");var subQ2=makeQuery(id+"F3.imprint","INTERSECT",VERTEX,{"derivedFrom":[subQ1,subQ0]});Q50=makeQuery(id+"F3.imprint","IMPRINT",FACE,{"disambiguationData":[TD([[makeQuery(id+"F3.imprint","IMPRINT",EDGE,{"disambiguationData":[TD([[subQ2,1.0]])],"derivedFrom":subQ1}),1.0]])]});}
            var Q51;
            {var subQ4=sQuery(id+"F3.wireOp",EDGE,"E6.0.5");var subQ6=sQuery(id+"F3.wireOp",EDGE,"E6.0.4");var subQ7=makeQuery(id+"F3.imprint","INTERSECT",VERTEX,{"derivedFrom":[subQ6,subQ4]});Q51=makeQuery(id+"F3.imprint","IMPRINT",FACE,{"disambiguationData":[TD([[makeQuery(id+"F3.imprint","IMPRINT",EDGE,{"disambiguationData":[TD([[subQ7,1.0]])],"derivedFrom":subQ6}),1.0]])]});}
            extrude(context, id + "F4", {"entities" : qUnion([Q0, Q1, Q2, Q3, Q4, Q5, Q6, Q7, Q8, Q9, Q10, Q11, Q12, Q13, Q14, Q15, Q16, Q17, Q18, Q19, Q20, Q21, Q22, Q23, Q24, Q25, Q26, Q27, Q28, Q29, Q30, Q31, Q32, Q33, Q34, Q35, Q36, Q37, Q38, Q39, Q40, Q41, Q42, Q43, Q44, Q45, Q46, Q47, Q48, Q49, Q50, Q51]), "operationType" : NewBodyOperationType.ADD, "oppositeDirection" : true, "depth" : 5 * mm});
        }
        {
            var Q0;
            {var subQ4=sQuery(id+"F0.wireOp",EDGE,"E0");var subQ5=sQuery(id+"F0.wireOp",EDGE,"E3.filletArc");var subQ23=sQuery(id+"F0.wireOp",EDGE,"E5.filletArc");Q0=makeQuery(id+"F4.boolean.opBoolean","SPLIT",FACE,{"disambiguationData":[TD([makeQuery(id+"F2.opShell","OFFSET_FACE",FACE,{"disambiguationData":[OSD([subQ4])]})])],"derivedFrom":makeQuery(id+"F2.opShell","OFFSET_FACE",FACE,{"disambiguationData":[OSD([subQ4,sQuery(id+"F0.wireOp",EDGE,"E1"),sQuery(id+"F0.wireOp",EDGE,"E2"),subQ5,sQuery(id+"F0.wireOp",EDGE,"E4.filletArc"),subQ23])]})});}
            var sketch = newSketch(context, id + "F5", { "sketchPlane" : qUnion([Q0])});
            skLineSegment(sketch, "E49", {"start": v(0, 128.17) * mm, "end": v(-54.63, 96.63) * mm});
            skLineSegment(sketch, "E50.1.0.0", {"start": v(-4.04, 135.08) * mm, "end": v(-58.67, 103.53) * mm});
            skLineSegment(sketch, "E50.2.0.0", {"start": v(-8.08, 141.98) * mm, "end": v(-62.71, 110.44) * mm});
            skLineSegment(sketch, "E50.3.0.0", {"start": v(-12.12, 148.89) * mm, "end": v(-66.75, 117.35) * mm});
            skLineSegment(sketch, "E50.4.0.0", {"start": v(-16.16, 155.8) * mm, "end": v(-70.8, 124.25) * mm});
            skLineSegment(sketch, "E50.5.0.0", {"start": v(-20.2, 162.7) * mm, "end": v(-74.83, 131.16) * mm});
            skLineSegment(sketch, "E50.6.0.0", {"start": v(-24.23, 169.6) * mm, "end": v(-78.87, 138.06) * mm});
            skLineSegment(sketch, "E50.7.0.0", {"start": v(-28.27, 176.5) * mm, "end": v(-82.9, 144.97) * mm});
            skLineSegment(sketch, "E50.8.0.0", {"start": v(-32.31, 183.42) * mm, "end": v(-86.95, 151.87) * mm});
            skLineSegment(sketch, "E50.9.0.0", {"start": v(-36.35, 190.32) * mm, "end": v(-90.99, 158.78) * mm});
            skLineSegment(sketch, "E50.10.0.0", {"start": v(-40.4, 197.23) * mm, "end": v(-95.03, 165.68) * mm});
            skLineSegment(sketch, "E50.11.0.0", {"start": v(-44.43, 204.13) * mm, "end": v(-99.06, 172.59) * mm});
            skLineSegment(sketch, "E50.12.0.0", {"start": v(-48.47, 211.04) * mm, "end": v(-103.1, 179.5) * mm});
            skLineSegment(sketch, "E50.13.0.0", {"start": v(-52.5, 217.94) * mm, "end": v(-107.14, 186.4) * mm});
            skLineSegment(sketch, "E50.direction1", {"start": v(-54.63, 96.63) * mm, "end": v(-58.67, 103.53) * mm, "construction": true});
            skSolve(sketch);
        }
        {
            var Q0;
            {var subQ0=sQuery(id+"F5.wireOp",EDGE,"E49");var subQ1=sQuery(id+"F0.wireOp",EDGE,"E3.filletArc");var subQ2=sQuery(id+"F0.wireOp",EDGE,"E0");var subQ3=makeQuery(id+"F2.opShell","OFFSET_FACE",FACE,{"disambiguationData":[OSD([subQ2,sQuery(id+"F0.wireOp",EDGE,"E1"),sQuery(id+"F0.wireOp",EDGE,"E2"),subQ1,sQuery(id+"F0.wireOp",EDGE,"E4.filletArc"),sQuery(id+"F0.wireOp",EDGE,"E5.filletArc")])]});var subQ6=makeQuery(id+"F4.opExtrude","SWEPT_FACE",FACE,{"disambiguationData":[OSD([sQuery(id+"F3.wireOp",EDGE,"E11.6.0.0")])]});var subQ7=makeQuery(id+"F5.imprint","INTERSECT",VERTEX,{"derivedFrom":[makeQuery(id+"F4.boolean.opBoolean","INTERSECT",EDGE,{"derivedFrom":[subQ3,subQ6]}),subQ0]});var subQ29=makeQuery(id+"F5.imprint","INTERSECT",VERTEX,{"derivedFrom":[makeQuery(id+"F4.boolean.opBoolean","INTERSECT",EDGE,{"derivedFrom":[subQ3,makeQuery(id+"F4.opExtrude","SWEPT_FACE",FACE,{"disambiguationData":[OSD([sQuery(id+"F3.wireOp",EDGE,"E11.5.0.0")])]})]}),subQ0]});Q0=makeQuery(id+"F5.imprint","IMPRINT",FACE,{"disambiguationData":[TD([[makeQuery(id+"F5.imprint","IMPRINT",EDGE,{"disambiguationData":[TD([[subQ29,1.0],[subQ7,-1.0]])],"derivedFrom":subQ0}),1.0]])]});}
            var Q1;
            {var subQ0=sQuery(id+"F5.wireOp",EDGE,"E50.2.0.0");var subQ15=sQuery(id+"F0.wireOp",EDGE,"E3.filletArc");var subQ16=sQuery(id+"F0.wireOp",EDGE,"E0");var subQ20=makeQuery(id+"F4.boolean.opBoolean","SPLIT",EDGE,{"disambiguationData":[TD([makeQuery(id+"F2.opShell","OFFSET_FACE",FACE,{"disambiguationData":[OSD([subQ15])]})])],"derivedFrom":makeQuery(id+"F2.opShell","OFFSET_EDGE",EDGE,{"disambiguationData":[OSD([subQ16]),TDD([makeQuery(id+"F1.opExtrude","CAP_EDGE",EDGE,{"disambiguationData":[OSD([subQ16])],"isStart":false})])]})});var subQ21=makeQuery(id+"F5.imprint","INTERSECT",VERTEX,{"derivedFrom":[subQ20,subQ0]});Q1=makeQuery(id+"F5.imprint","IMPRINT",FACE,{"disambiguationData":[TD([[makeQuery(id+"F5.imprint","IMPRINT",EDGE,{"disambiguationData":[TD([[subQ21,-1.0]])],"derivedFrom":subQ20}),-1.0]])]});}
            var Q2;
            {var subQ0=sQuery(id+"F5.wireOp",EDGE,"E50.4.0.0");var subQ15=sQuery(id+"F0.wireOp",EDGE,"E3.filletArc");var subQ16=sQuery(id+"F0.wireOp",EDGE,"E0");var subQ20=makeQuery(id+"F4.boolean.opBoolean","SPLIT",EDGE,{"disambiguationData":[TD([makeQuery(id+"F2.opShell","OFFSET_FACE",FACE,{"disambiguationData":[OSD([subQ15])]})])],"derivedFrom":makeQuery(id+"F2.opShell","OFFSET_EDGE",EDGE,{"disambiguationData":[OSD([subQ16]),TDD([makeQuery(id+"F1.opExtrude","CAP_EDGE",EDGE,{"disambiguationData":[OSD([subQ16])],"isStart":false})])]})});var subQ21=makeQuery(id+"F5.imprint","INTERSECT",VERTEX,{"derivedFrom":[subQ20,subQ0]});Q2=makeQuery(id+"F5.imprint","IMPRINT",FACE,{"disambiguationData":[TD([[makeQuery(id+"F5.imprint","IMPRINT",EDGE,{"disambiguationData":[TD([[subQ21,-1.0]])],"derivedFrom":subQ20}),-1.0]])]});}
            var Q3;
            {var subQ0=sQuery(id+"F5.wireOp",EDGE,"E50.6.0.0");var subQ15=sQuery(id+"F0.wireOp",EDGE,"E3.filletArc");var subQ16=sQuery(id+"F0.wireOp",EDGE,"E0");var subQ20=makeQuery(id+"F4.boolean.opBoolean","SPLIT",EDGE,{"disambiguationData":[TD([makeQuery(id+"F2.opShell","OFFSET_FACE",FACE,{"disambiguationData":[OSD([subQ15])]})])],"derivedFrom":makeQuery(id+"F2.opShell","OFFSET_EDGE",EDGE,{"disambiguationData":[OSD([subQ16]),TDD([makeQuery(id+"F1.opExtrude","CAP_EDGE",EDGE,{"disambiguationData":[OSD([subQ16])],"isStart":false})])]})});var subQ21=makeQuery(id+"F5.imprint","INTERSECT",VERTEX,{"derivedFrom":[subQ20,subQ0]});Q3=makeQuery(id+"F5.imprint","IMPRINT",FACE,{"disambiguationData":[TD([[makeQuery(id+"F5.imprint","IMPRINT",EDGE,{"disambiguationData":[TD([[subQ21,-1.0]])],"derivedFrom":subQ20}),-1.0]])]});}
            var Q4;
            {var subQ0=sQuery(id+"F5.wireOp",EDGE,"E50.8.0.0");var subQ15=sQuery(id+"F0.wireOp",EDGE,"E3.filletArc");var subQ16=sQuery(id+"F0.wireOp",EDGE,"E0");var subQ20=makeQuery(id+"F4.boolean.opBoolean","SPLIT",EDGE,{"disambiguationData":[TD([makeQuery(id+"F2.opShell","OFFSET_FACE",FACE,{"disambiguationData":[OSD([subQ15])]})])],"derivedFrom":makeQuery(id+"F2.opShell","OFFSET_EDGE",EDGE,{"disambiguationData":[OSD([subQ16]),TDD([makeQuery(id+"F1.opExtrude","CAP_EDGE",EDGE,{"disambiguationData":[OSD([subQ16])],"isStart":false})])]})});var subQ21=makeQuery(id+"F5.imprint","INTERSECT",VERTEX,{"derivedFrom":[subQ20,subQ0]});Q4=makeQuery(id+"F5.imprint","IMPRINT",FACE,{"disambiguationData":[TD([[makeQuery(id+"F5.imprint","IMPRINT",EDGE,{"disambiguationData":[TD([[subQ21,-1.0]])],"derivedFrom":subQ20}),-1.0]])]});}
            var Q5;
            {var subQ0=sQuery(id+"F5.wireOp",EDGE,"E50.10.0.0");var subQ15=sQuery(id+"F0.wireOp",EDGE,"E3.filletArc");var subQ16=sQuery(id+"F0.wireOp",EDGE,"E0");var subQ20=makeQuery(id+"F4.boolean.opBoolean","SPLIT",EDGE,{"disambiguationData":[TD([makeQuery(id+"F2.opShell","OFFSET_FACE",FACE,{"disambiguationData":[OSD([subQ15])]})])],"derivedFrom":makeQuery(id+"F2.opShell","OFFSET_EDGE",EDGE,{"disambiguationData":[OSD([subQ16]),TDD([makeQuery(id+"F1.opExtrude","CAP_EDGE",EDGE,{"disambiguationData":[OSD([subQ16])],"isStart":false})])]})});var subQ21=makeQuery(id+"F5.imprint","INTERSECT",VERTEX,{"derivedFrom":[subQ20,subQ0]});Q5=makeQuery(id+"F5.imprint","IMPRINT",FACE,{"disambiguationData":[TD([[makeQuery(id+"F5.imprint","IMPRINT",EDGE,{"disambiguationData":[TD([[subQ21,-1.0]])],"derivedFrom":subQ20}),-1.0]])]});}
            var Q6;
            {var subQ1=sQuery(id+"F0.wireOp",EDGE,"E3.filletArc");var subQ4=makeQuery(id+"F2.opShell","OFFSET_EDGE",EDGE,{"disambiguationData":[OSD([subQ1]),TDD([makeQuery(id+"F1.opExtrude","CAP_EDGE",EDGE,{"disambiguationData":[OSD([subQ1])],"isStart":false})])]});var subQ6=sQuery(id+"F5.wireOp",EDGE,"E50.13.0.0");var subQ7=makeQuery(id+"F5.imprint","INTERSECT",VERTEX,{"derivedFrom":[subQ4,subQ6]});Q6=makeQuery(id+"F5.imprint","IMPRINT",FACE,{"disambiguationData":[TD([[makeQuery(id+"F5.imprint","IMPRINT",EDGE,{"disambiguationData":[TD([[subQ7,1.0]])],"derivedFrom":subQ4}),-1.0]])]});}
            var Q7;
            Q7=makeQuery(id+"F4.opExtrude","CAP_FACE",FACE,{"disambiguationData":[OSD([sQuery(id+"F3.wireOp",EDGE,"E6.0.0"),sQuery(id+"F3.wireOp",EDGE,"E6.0.2"),sQuery(id+"F3.wireOp",EDGE,"E6.0.3"),sQuery(id+"F3.wireOp",EDGE,"E6.0.5"),sQuery(id+"F3.wireOp",EDGE,"E7"),sQuery(id+"F3.wireOp",EDGE,"E9"),sQuery(id+"F3.wireOp",EDGE,"E10.1.0.0"),sQuery(id+"F3.wireOp",EDGE,"E10.2.0.0"),sQuery(id+"F3.wireOp",EDGE,"E10.3.0.0"),sQuery(id+"F3.wireOp",EDGE,"E10.4.0.0"),sQuery(id+"F3.wireOp",EDGE,"E10.5.0.0"),sQuery(id+"F3.wireOp",EDGE,"E10.6.0.0"),sQuery(id+"F3.wireOp",EDGE,"E25.1.0.0")])],"isStart":false});
            extrude(context, id + "F6", {"entities" : qUnion([Q0, Q1, Q2, Q3, Q4, Q5, Q6]), "operationType" : NewBodyOperationType.ADD, "endBound" : BoundingType.UP_TO_SURFACE, "endBoundEntityFace" : qUnion([Q7]), "depth" : 5 * mm});
        }
        {
            var Q0;
            Q0=makeQuery(id+"F4.opExtrude","CAP_EDGE",EDGE,{"disambiguationData":[OSD([sQuery(id+"F3.wireOp",EDGE,"E25.1.0.0")])],"isStart":false});
            var Q1;
            Q1=makeQuery(id+"F4.opExtrude","CAP_EDGE",EDGE,{"disambiguationData":[OSD([sQuery(id+"F3.wireOp",EDGE,"E25.2.0.0")])],"isStart":false});
            var Q2;
            Q2=makeQuery(id+"F4.opExtrude","CAP_EDGE",EDGE,{"disambiguationData":[OSD([sQuery(id+"F3.wireOp",EDGE,"E25.3.0.0")])],"isStart":false});
            var Q3;
            Q3=makeQuery(id+"F4.opExtrude","CAP_EDGE",EDGE,{"disambiguationData":[OSD([sQuery(id+"F3.wireOp",EDGE,"E25.4.0.0")])],"isStart":false});
            var Q4;
            Q4=makeQuery(id+"F4.opExtrude","CAP_EDGE",EDGE,{"disambiguationData":[OSD([sQuery(id+"F3.wireOp",EDGE,"E25.5.0.0")])],"isStart":false});
            var Q5;
            Q5=makeQuery(id+"F4.opExtrude","CAP_EDGE",EDGE,{"disambiguationData":[OSD([sQuery(id+"F3.wireOp",EDGE,"E25.6.0.0")])],"isStart":false});
            var Q6;
            Q6=makeQuery(id+"F4.opExtrude","CAP_EDGE",EDGE,{"disambiguationData":[OSD([sQuery(id+"F3.wireOp",EDGE,"E25.7.0.0")])],"isStart":false});
            var Q7;
            Q7=makeQuery(id+"F4.opExtrude","CAP_EDGE",EDGE,{"disambiguationData":[OSD([sQuery(id+"F3.wireOp",EDGE,"E25.8.0.0")])],"isStart":false});
            var Q8;
            Q8=makeQuery(id+"F4.opExtrude","CAP_EDGE",EDGE,{"disambiguationData":[OSD([sQuery(id+"F3.wireOp",EDGE,"E25.9.0.0")])],"isStart":false});
            var Q9;
            Q9=makeQuery(id+"F4.opExtrude","CAP_EDGE",EDGE,{"disambiguationData":[OSD([sQuery(id+"F3.wireOp",EDGE,"E25.10.0.0")])],"isStart":false});
            var Q10;
            Q10=makeQuery(id+"F4.opExtrude","CAP_EDGE",EDGE,{"disambiguationData":[OSD([sQuery(id+"F3.wireOp",EDGE,"E25.11.0.0")])],"isStart":false});
            var Q11;
            Q11=makeQuery(id+"F4.opExtrude","CAP_EDGE",EDGE,{"disambiguationData":[OSD([sQuery(id+"F3.wireOp",EDGE,"E25.12.0.0")])],"isStart":false});
            var Q12;
            Q12=makeQuery(id+"F4.opExtrude","CAP_EDGE",EDGE,{"disambiguationData":[OSD([sQuery(id+"F3.wireOp",EDGE,"E25.13.0.0")])],"isStart":false});
            var Q13;
            Q13=makeQuery(id+"F6.opExtrude","CAP_EDGE",EDGE,{"disambiguationData":[OSD([sQuery(id+"F5.wireOp",EDGE,"E50.13.0.0")])],"isStart":false});
            var Q14;
            Q14=makeQuery(id+"F6.opExtrude","CAP_EDGE",EDGE,{"disambiguationData":[OSD([sQuery(id+"F5.wireOp",EDGE,"E50.12.0.0")])],"isStart":false});
            var Q15;
            Q15=makeQuery(id+"F6.opExtrude","CAP_EDGE",EDGE,{"disambiguationData":[OSD([sQuery(id+"F5.wireOp",EDGE,"E50.11.0.0")])],"isStart":false});
            var Q16;
            Q16=makeQuery(id+"F6.opExtrude","CAP_EDGE",EDGE,{"disambiguationData":[OSD([sQuery(id+"F5.wireOp",EDGE,"E50.10.0.0")])],"isStart":false});
            var Q17;
            {var subQ0=sQuery(id+"F3.wireOp",EDGE,"E7");var subQ9=sQuery(id+"F3.wireOp",EDGE,"E6.0.2");var subQ11=makeQuery(id+"F3.imprint","IMPRINT",EDGE,{"disambiguationData":[TD([[makeQuery(id+"F3.imprint","INTERSECT",VERTEX,{"derivedFrom":[subQ9,subQ0]}),1.0]])],"derivedFrom":subQ0});var subQ12=makeQuery(id+"F3.imprint","IMPRINT",VERTEX,{"disambiguationData":[OD(11.0)],"derivedFrom":subQ0});var subQ13=makeQuery(id+"F3.imprint","IMPRINT",EDGE,{"disambiguationData":[TD([[subQ12,-1.0]])],"derivedFrom":subQ0});var subQ14=makeQuery(id+"F3.imprint","IMPRINT",VERTEX,{"disambiguationData":[OD(10.0)],"derivedFrom":subQ0});var subQ15=makeQuery(id+"F3.imprint","IMPRINT",EDGE,{"disambiguationData":[TD([[subQ14,-1.0]])],"derivedFrom":subQ0});var subQ16=makeQuery(id+"F3.imprint","IMPRINT",VERTEX,{"disambiguationData":[OD(9.0)],"derivedFrom":subQ0});var subQ17=makeQuery(id+"F3.imprint","IMPRINT",EDGE,{"disambiguationData":[TD([[subQ16,-1.0]])],"derivedFrom":subQ0});var subQ18=makeQuery(id+"F3.imprint","IMPRINT",VERTEX,{"disambiguationData":[OD(8.0)],"derivedFrom":subQ0});var subQ19=makeQuery(id+"F3.imprint","IMPRINT",EDGE,{"disambiguationData":[TD([[subQ18,-1.0]])],"derivedFrom":subQ0});var subQ20=makeQuery(id+"F3.imprint","IMPRINT",VERTEX,{"disambiguationData":[OD(7.0)],"derivedFrom":subQ0});var subQ21=makeQuery(id+"F3.imprint","IMPRINT",EDGE,{"disambiguationData":[TD([[subQ20,-1.0]])],"derivedFrom":subQ0});var subQ22=makeQuery(id+"F3.imprint","IMPRINT",VERTEX,{"disambiguationData":[OD(6.0)],"derivedFrom":subQ0});var subQ23=makeQuery(id+"F3.imprint","IMPRINT",EDGE,{"disambiguationData":[TD([[subQ22,-1.0]])],"derivedFrom":subQ0});var subQ24=makeQuery(id+"F3.imprint","IMPRINT",VERTEX,{"disambiguationData":[OD(5.0)],"derivedFrom":subQ0});var subQ25=makeQuery(id+"F3.imprint","IMPRINT",EDGE,{"disambiguationData":[TD([[subQ24,-1.0]])],"derivedFrom":subQ0});var subQ26=makeQuery(id+"F3.imprint","IMPRINT",VERTEX,{"disambiguationData":[OD(4.0)],"derivedFrom":subQ0});var subQ27=makeQuery(id+"F3.imprint","IMPRINT",EDGE,{"disambiguationData":[TD([[subQ26,-1.0]])],"derivedFrom":subQ0});var subQ28=makeQuery(id+"F3.imprint","IMPRINT",VERTEX,{"disambiguationData":[OD(3.0)],"derivedFrom":subQ0});var subQ29=makeQuery(id+"F3.imprint","IMPRINT",EDGE,{"disambiguationData":[TD([[subQ28,-1.0]])],"derivedFrom":subQ0});var subQ30=makeQuery(id+"F3.imprint","IMPRINT",VERTEX,{"disambiguationData":[OD(2.0)],"derivedFrom":subQ0});var subQ31=makeQuery(id+"F3.imprint","IMPRINT",EDGE,{"disambiguationData":[TD([[subQ30,-1.0]])],"derivedFrom":subQ0});var subQ32=makeQuery(id+"F3.imprint","IMPRINT",VERTEX,{"disambiguationData":[OD(1.0)],"derivedFrom":subQ0});var subQ33=makeQuery(id+"F3.imprint","IMPRINT",EDGE,{"disambiguationData":[TD([[subQ32,-1.0]])],"derivedFrom":subQ0});var subQ34=makeQuery(id+"F3.imprint","IMPRINT",VERTEX,{"disambiguationData":[OD(0.0)],"derivedFrom":subQ0});var subQ35=makeQuery(id+"F3.imprint","IMPRINT",EDGE,{"disambiguationData":[TD([[subQ34,-1.0]])],"derivedFrom":subQ0});var subQ37=makeQuery(id+"F3.imprint","IMPRINT",EDGE,{"disambiguationData":[TD([[subQ34,1.0]])],"derivedFrom":subQ0});var subQ38=sQuery(id+"F5.wireOp",EDGE,"E50.11.0.0");Q17=makeQuery(id+"F6.boolean.opBoolean","SPLIT",EDGE,{"disambiguationData":[TD([makeQuery(id+"F6.opExtrude","SWEPT_FACE",FACE,{"disambiguationData":[OSD([subQ38])]})])],"derivedFrom":makeQuery(id+"F4.opExtrude","CAP_EDGE",EDGE,{"disambiguationData":[OSD([subQ0]),TDD([subQ37,subQ35,subQ33,subQ31,subQ29,subQ27,subQ25,subQ23,subQ21,subQ19,subQ17,subQ15,subQ13,subQ11])],"isStart":false})});}
            var Q18;
            {var subQ0=sQuery(id+"F3.wireOp",EDGE,"E7");var subQ3=sQuery(id+"F0.wireOp",EDGE,"E3.filletArc");var subQ9=sQuery(id+"F3.wireOp",EDGE,"E6.0.2");var subQ11=makeQuery(id+"F3.imprint","IMPRINT",EDGE,{"disambiguationData":[TD([[makeQuery(id+"F3.imprint","INTERSECT",VERTEX,{"derivedFrom":[subQ9,subQ0]}),1.0]])],"derivedFrom":subQ0});var subQ12=makeQuery(id+"F3.imprint","IMPRINT",VERTEX,{"disambiguationData":[OD(11.0)],"derivedFrom":subQ0});var subQ13=makeQuery(id+"F3.imprint","IMPRINT",EDGE,{"disambiguationData":[TD([[subQ12,-1.0]])],"derivedFrom":subQ0});var subQ14=makeQuery(id+"F3.imprint","IMPRINT",VERTEX,{"disambiguationData":[OD(10.0)],"derivedFrom":subQ0});var subQ15=makeQuery(id+"F3.imprint","IMPRINT",EDGE,{"disambiguationData":[TD([[subQ14,-1.0]])],"derivedFrom":subQ0});var subQ16=makeQuery(id+"F3.imprint","IMPRINT",VERTEX,{"disambiguationData":[OD(9.0)],"derivedFrom":subQ0});var subQ17=makeQuery(id+"F3.imprint","IMPRINT",EDGE,{"disambiguationData":[TD([[subQ16,-1.0]])],"derivedFrom":subQ0});var subQ18=makeQuery(id+"F3.imprint","IMPRINT",VERTEX,{"disambiguationData":[OD(8.0)],"derivedFrom":subQ0});var subQ19=makeQuery(id+"F3.imprint","IMPRINT",EDGE,{"disambiguationData":[TD([[subQ18,-1.0]])],"derivedFrom":subQ0});var subQ20=makeQuery(id+"F3.imprint","IMPRINT",VERTEX,{"disambiguationData":[OD(7.0)],"derivedFrom":subQ0});var subQ21=makeQuery(id+"F3.imprint","IMPRINT",EDGE,{"disambiguationData":[TD([[subQ20,-1.0]])],"derivedFrom":subQ0});var subQ22=makeQuery(id+"F3.imprint","IMPRINT",VERTEX,{"disambiguationData":[OD(6.0)],"derivedFrom":subQ0});var subQ23=makeQuery(id+"F3.imprint","IMPRINT",EDGE,{"disambiguationData":[TD([[subQ22,-1.0]])],"derivedFrom":subQ0});var subQ24=makeQuery(id+"F3.imprint","IMPRINT",VERTEX,{"disambiguationData":[OD(5.0)],"derivedFrom":subQ0});var subQ25=makeQuery(id+"F3.imprint","IMPRINT",EDGE,{"disambiguationData":[TD([[subQ24,-1.0]])],"derivedFrom":subQ0});var subQ26=makeQuery(id+"F3.imprint","IMPRINT",VERTEX,{"disambiguationData":[OD(4.0)],"derivedFrom":subQ0});var subQ27=makeQuery(id+"F3.imprint","IMPRINT",EDGE,{"disambiguationData":[TD([[subQ26,-1.0]])],"derivedFrom":subQ0});var subQ28=makeQuery(id+"F3.imprint","IMPRINT",VERTEX,{"disambiguationData":[OD(3.0)],"derivedFrom":subQ0});var subQ29=makeQuery(id+"F3.imprint","IMPRINT",EDGE,{"disambiguationData":[TD([[subQ28,-1.0]])],"derivedFrom":subQ0});var subQ30=makeQuery(id+"F3.imprint","IMPRINT",VERTEX,{"disambiguationData":[OD(2.0)],"derivedFrom":subQ0});var subQ31=makeQuery(id+"F3.imprint","IMPRINT",EDGE,{"disambiguationData":[TD([[subQ30,-1.0]])],"derivedFrom":subQ0});var subQ32=makeQuery(id+"F3.imprint","IMPRINT",VERTEX,{"disambiguationData":[OD(1.0)],"derivedFrom":subQ0});var subQ33=makeQuery(id+"F3.imprint","IMPRINT",EDGE,{"disambiguationData":[TD([[subQ32,-1.0]])],"derivedFrom":subQ0});var subQ34=makeQuery(id+"F3.imprint","IMPRINT",VERTEX,{"disambiguationData":[OD(0.0)],"derivedFrom":subQ0});var subQ35=makeQuery(id+"F3.imprint","IMPRINT",EDGE,{"disambiguationData":[TD([[subQ34,-1.0]])],"derivedFrom":subQ0});var subQ37=makeQuery(id+"F3.imprint","IMPRINT",EDGE,{"disambiguationData":[TD([[subQ34,1.0]])],"derivedFrom":subQ0});Q18=makeQuery(id+"F6.boolean.opBoolean","SPLIT",EDGE,{"disambiguationData":[TD([makeQuery(id+"F2.opShell","OFFSET_FACE",FACE,{"disambiguationData":[OSD([subQ3])]})])],"derivedFrom":makeQuery(id+"F4.opExtrude","CAP_EDGE",EDGE,{"disambiguationData":[OSD([subQ0]),TDD([subQ37,subQ35,subQ33,subQ31,subQ29,subQ27,subQ25,subQ23,subQ21,subQ19,subQ17,subQ15,subQ13,subQ11])],"isStart":false})});}
            var Q19;
            {var subQ0=sQuery(id+"F5.wireOp",EDGE,"E50.9.0.0");var subQ1=sQuery(id+"F3.wireOp",EDGE,"E7");var subQ10=sQuery(id+"F3.wireOp",EDGE,"E6.0.2");var subQ12=makeQuery(id+"F3.imprint","IMPRINT",EDGE,{"disambiguationData":[TD([[makeQuery(id+"F3.imprint","INTERSECT",VERTEX,{"derivedFrom":[subQ10,subQ1]}),1.0]])],"derivedFrom":subQ1});var subQ13=makeQuery(id+"F3.imprint","IMPRINT",VERTEX,{"disambiguationData":[OD(11.0)],"derivedFrom":subQ1});var subQ14=makeQuery(id+"F3.imprint","IMPRINT",EDGE,{"disambiguationData":[TD([[subQ13,-1.0]])],"derivedFrom":subQ1});var subQ15=makeQuery(id+"F3.imprint","IMPRINT",VERTEX,{"disambiguationData":[OD(10.0)],"derivedFrom":subQ1});var subQ16=makeQuery(id+"F3.imprint","IMPRINT",EDGE,{"disambiguationData":[TD([[subQ15,-1.0]])],"derivedFrom":subQ1});var subQ17=makeQuery(id+"F3.imprint","IMPRINT",VERTEX,{"disambiguationData":[OD(9.0)],"derivedFrom":subQ1});var subQ18=makeQuery(id+"F3.imprint","IMPRINT",EDGE,{"disambiguationData":[TD([[subQ17,-1.0]])],"derivedFrom":subQ1});var subQ19=makeQuery(id+"F3.imprint","IMPRINT",VERTEX,{"disambiguationData":[OD(8.0)],"derivedFrom":subQ1});var subQ20=makeQuery(id+"F3.imprint","IMPRINT",EDGE,{"disambiguationData":[TD([[subQ19,-1.0]])],"derivedFrom":subQ1});var subQ21=makeQuery(id+"F3.imprint","IMPRINT",VERTEX,{"disambiguationData":[OD(7.0)],"derivedFrom":subQ1});var subQ22=makeQuery(id+"F3.imprint","IMPRINT",EDGE,{"disambiguationData":[TD([[subQ21,-1.0]])],"derivedFrom":subQ1});var subQ23=makeQuery(id+"F3.imprint","IMPRINT",VERTEX,{"disambiguationData":[OD(6.0)],"derivedFrom":subQ1});var subQ24=makeQuery(id+"F3.imprint","IMPRINT",EDGE,{"disambiguationData":[TD([[subQ23,-1.0]])],"derivedFrom":subQ1});var subQ25=makeQuery(id+"F3.imprint","IMPRINT",VERTEX,{"disambiguationData":[OD(5.0)],"derivedFrom":subQ1});var subQ26=makeQuery(id+"F3.imprint","IMPRINT",EDGE,{"disambiguationData":[TD([[subQ25,-1.0]])],"derivedFrom":subQ1});var subQ27=makeQuery(id+"F3.imprint","IMPRINT",VERTEX,{"disambiguationData":[OD(4.0)],"derivedFrom":subQ1});var subQ28=makeQuery(id+"F3.imprint","IMPRINT",EDGE,{"disambiguationData":[TD([[subQ27,-1.0]])],"derivedFrom":subQ1});var subQ29=makeQuery(id+"F3.imprint","IMPRINT",VERTEX,{"disambiguationData":[OD(3.0)],"derivedFrom":subQ1});var subQ30=makeQuery(id+"F3.imprint","IMPRINT",EDGE,{"disambiguationData":[TD([[subQ29,-1.0]])],"derivedFrom":subQ1});var subQ31=makeQuery(id+"F3.imprint","IMPRINT",VERTEX,{"disambiguationData":[OD(2.0)],"derivedFrom":subQ1});var subQ32=makeQuery(id+"F3.imprint","IMPRINT",EDGE,{"disambiguationData":[TD([[subQ31,-1.0]])],"derivedFrom":subQ1});var subQ33=makeQuery(id+"F3.imprint","IMPRINT",VERTEX,{"disambiguationData":[OD(1.0)],"derivedFrom":subQ1});var subQ34=makeQuery(id+"F3.imprint","IMPRINT",EDGE,{"disambiguationData":[TD([[subQ33,-1.0]])],"derivedFrom":subQ1});var subQ35=makeQuery(id+"F3.imprint","IMPRINT",VERTEX,{"disambiguationData":[OD(0.0)],"derivedFrom":subQ1});var subQ36=makeQuery(id+"F3.imprint","IMPRINT",EDGE,{"disambiguationData":[TD([[subQ35,-1.0]])],"derivedFrom":subQ1});var subQ38=makeQuery(id+"F3.imprint","IMPRINT",EDGE,{"disambiguationData":[TD([[subQ35,1.0]])],"derivedFrom":subQ1});Q19=makeQuery(id+"F6.boolean.opBoolean","SPLIT",EDGE,{"disambiguationData":[TD([makeQuery(id+"F6.opExtrude","SWEPT_FACE",FACE,{"disambiguationData":[OSD([subQ0])]})])],"derivedFrom":makeQuery(id+"F4.opExtrude","CAP_EDGE",EDGE,{"disambiguationData":[OSD([subQ1]),TDD([subQ38,subQ36,subQ34,subQ32,subQ30,subQ28,subQ26,subQ24,subQ22,subQ20,subQ18,subQ16,subQ14,subQ12])],"isStart":false})});}
            var Q20;
            Q20=makeQuery(id+"F6.opExtrude","CAP_EDGE",EDGE,{"disambiguationData":[OSD([sQuery(id+"F5.wireOp",EDGE,"E50.9.0.0")])],"isStart":false});
            var Q21;
            Q21=makeQuery(id+"F6.opExtrude","CAP_EDGE",EDGE,{"disambiguationData":[OSD([sQuery(id+"F5.wireOp",EDGE,"E50.8.0.0")])],"isStart":false});
            var Q22;
            {var subQ0=sQuery(id+"F5.wireOp",EDGE,"E50.7.0.0");var subQ3=sQuery(id+"F3.wireOp",EDGE,"E7");var subQ10=sQuery(id+"F3.wireOp",EDGE,"E6.0.2");var subQ12=makeQuery(id+"F3.imprint","IMPRINT",EDGE,{"disambiguationData":[TD([[makeQuery(id+"F3.imprint","INTERSECT",VERTEX,{"derivedFrom":[subQ10,subQ3]}),1.0]])],"derivedFrom":subQ3});var subQ13=makeQuery(id+"F3.imprint","IMPRINT",VERTEX,{"disambiguationData":[OD(11.0)],"derivedFrom":subQ3});var subQ14=makeQuery(id+"F3.imprint","IMPRINT",EDGE,{"disambiguationData":[TD([[subQ13,-1.0]])],"derivedFrom":subQ3});var subQ15=makeQuery(id+"F3.imprint","IMPRINT",VERTEX,{"disambiguationData":[OD(10.0)],"derivedFrom":subQ3});var subQ16=makeQuery(id+"F3.imprint","IMPRINT",EDGE,{"disambiguationData":[TD([[subQ15,-1.0]])],"derivedFrom":subQ3});var subQ17=makeQuery(id+"F3.imprint","IMPRINT",VERTEX,{"disambiguationData":[OD(9.0)],"derivedFrom":subQ3});var subQ18=makeQuery(id+"F3.imprint","IMPRINT",EDGE,{"disambiguationData":[TD([[subQ17,-1.0]])],"derivedFrom":subQ3});var subQ19=makeQuery(id+"F3.imprint","IMPRINT",VERTEX,{"disambiguationData":[OD(8.0)],"derivedFrom":subQ3});var subQ20=makeQuery(id+"F3.imprint","IMPRINT",EDGE,{"disambiguationData":[TD([[subQ19,-1.0]])],"derivedFrom":subQ3});var subQ21=makeQuery(id+"F3.imprint","IMPRINT",VERTEX,{"disambiguationData":[OD(7.0)],"derivedFrom":subQ3});var subQ22=makeQuery(id+"F3.imprint","IMPRINT",EDGE,{"disambiguationData":[TD([[subQ21,-1.0]])],"derivedFrom":subQ3});var subQ23=makeQuery(id+"F3.imprint","IMPRINT",VERTEX,{"disambiguationData":[OD(6.0)],"derivedFrom":subQ3});var subQ24=makeQuery(id+"F3.imprint","IMPRINT",EDGE,{"disambiguationData":[TD([[subQ23,-1.0]])],"derivedFrom":subQ3});var subQ25=makeQuery(id+"F3.imprint","IMPRINT",VERTEX,{"disambiguationData":[OD(5.0)],"derivedFrom":subQ3});var subQ26=makeQuery(id+"F3.imprint","IMPRINT",EDGE,{"disambiguationData":[TD([[subQ25,-1.0]])],"derivedFrom":subQ3});var subQ27=makeQuery(id+"F3.imprint","IMPRINT",VERTEX,{"disambiguationData":[OD(4.0)],"derivedFrom":subQ3});var subQ28=makeQuery(id+"F3.imprint","IMPRINT",EDGE,{"disambiguationData":[TD([[subQ27,-1.0]])],"derivedFrom":subQ3});var subQ29=makeQuery(id+"F3.imprint","IMPRINT",VERTEX,{"disambiguationData":[OD(3.0)],"derivedFrom":subQ3});var subQ30=makeQuery(id+"F3.imprint","IMPRINT",EDGE,{"disambiguationData":[TD([[subQ29,-1.0]])],"derivedFrom":subQ3});var subQ31=makeQuery(id+"F3.imprint","IMPRINT",VERTEX,{"disambiguationData":[OD(2.0)],"derivedFrom":subQ3});var subQ32=makeQuery(id+"F3.imprint","IMPRINT",EDGE,{"disambiguationData":[TD([[subQ31,-1.0]])],"derivedFrom":subQ3});var subQ33=makeQuery(id+"F3.imprint","IMPRINT",VERTEX,{"disambiguationData":[OD(1.0)],"derivedFrom":subQ3});var subQ34=makeQuery(id+"F3.imprint","IMPRINT",EDGE,{"disambiguationData":[TD([[subQ33,-1.0]])],"derivedFrom":subQ3});var subQ35=makeQuery(id+"F3.imprint","IMPRINT",VERTEX,{"disambiguationData":[OD(0.0)],"derivedFrom":subQ3});var subQ36=makeQuery(id+"F3.imprint","IMPRINT",EDGE,{"disambiguationData":[TD([[subQ35,-1.0]])],"derivedFrom":subQ3});var subQ38=makeQuery(id+"F3.imprint","IMPRINT",EDGE,{"disambiguationData":[TD([[subQ35,1.0]])],"derivedFrom":subQ3});Q22=makeQuery(id+"F6.boolean.opBoolean","SPLIT",EDGE,{"disambiguationData":[TD([makeQuery(id+"F6.opExtrude","SWEPT_FACE",FACE,{"disambiguationData":[OSD([subQ0])]})])],"derivedFrom":makeQuery(id+"F4.opExtrude","CAP_EDGE",EDGE,{"disambiguationData":[OSD([subQ3]),TDD([subQ38,subQ36,subQ34,subQ32,subQ30,subQ28,subQ26,subQ24,subQ22,subQ20,subQ18,subQ16,subQ14,subQ12])],"isStart":false})});}
            var Q23;
            Q23=makeQuery(id+"F6.opExtrude","CAP_EDGE",EDGE,{"disambiguationData":[OSD([sQuery(id+"F5.wireOp",EDGE,"E50.7.0.0")])],"isStart":false});
            var Q24;
            Q24=makeQuery(id+"F6.opExtrude","CAP_EDGE",EDGE,{"disambiguationData":[OSD([sQuery(id+"F5.wireOp",EDGE,"E50.6.0.0")])],"isStart":false});
            var Q25;
            {var subQ2=sQuery(id+"F3.wireOp",EDGE,"E7");var subQ3=sQuery(id+"F3.wireOp",EDGE,"E6.0.2");var subQ4=sQuery(id+"F5.wireOp",EDGE,"E50.5.0.0");var subQ12=makeQuery(id+"F3.imprint","IMPRINT",EDGE,{"disambiguationData":[TD([[makeQuery(id+"F3.imprint","INTERSECT",VERTEX,{"derivedFrom":[subQ3,subQ2]}),1.0]])],"derivedFrom":subQ2});var subQ13=makeQuery(id+"F3.imprint","IMPRINT",VERTEX,{"disambiguationData":[OD(11.0)],"derivedFrom":subQ2});var subQ14=makeQuery(id+"F3.imprint","IMPRINT",EDGE,{"disambiguationData":[TD([[subQ13,-1.0]])],"derivedFrom":subQ2});var subQ15=makeQuery(id+"F3.imprint","IMPRINT",VERTEX,{"disambiguationData":[OD(10.0)],"derivedFrom":subQ2});var subQ16=makeQuery(id+"F3.imprint","IMPRINT",EDGE,{"disambiguationData":[TD([[subQ15,-1.0]])],"derivedFrom":subQ2});var subQ17=makeQuery(id+"F3.imprint","IMPRINT",VERTEX,{"disambiguationData":[OD(9.0)],"derivedFrom":subQ2});var subQ18=makeQuery(id+"F3.imprint","IMPRINT",EDGE,{"disambiguationData":[TD([[subQ17,-1.0]])],"derivedFrom":subQ2});var subQ19=makeQuery(id+"F3.imprint","IMPRINT",VERTEX,{"disambiguationData":[OD(8.0)],"derivedFrom":subQ2});var subQ20=makeQuery(id+"F3.imprint","IMPRINT",EDGE,{"disambiguationData":[TD([[subQ19,-1.0]])],"derivedFrom":subQ2});var subQ21=makeQuery(id+"F3.imprint","IMPRINT",VERTEX,{"disambiguationData":[OD(7.0)],"derivedFrom":subQ2});var subQ22=makeQuery(id+"F3.imprint","IMPRINT",EDGE,{"disambiguationData":[TD([[subQ21,-1.0]])],"derivedFrom":subQ2});var subQ23=makeQuery(id+"F3.imprint","IMPRINT",VERTEX,{"disambiguationData":[OD(6.0)],"derivedFrom":subQ2});var subQ24=makeQuery(id+"F3.imprint","IMPRINT",EDGE,{"disambiguationData":[TD([[subQ23,-1.0]])],"derivedFrom":subQ2});var subQ25=makeQuery(id+"F3.imprint","IMPRINT",VERTEX,{"disambiguationData":[OD(5.0)],"derivedFrom":subQ2});var subQ26=makeQuery(id+"F3.imprint","IMPRINT",EDGE,{"disambiguationData":[TD([[subQ25,-1.0]])],"derivedFrom":subQ2});var subQ27=makeQuery(id+"F3.imprint","IMPRINT",VERTEX,{"disambiguationData":[OD(4.0)],"derivedFrom":subQ2});var subQ28=makeQuery(id+"F3.imprint","IMPRINT",EDGE,{"disambiguationData":[TD([[subQ27,-1.0]])],"derivedFrom":subQ2});var subQ29=makeQuery(id+"F3.imprint","IMPRINT",VERTEX,{"disambiguationData":[OD(3.0)],"derivedFrom":subQ2});var subQ30=makeQuery(id+"F3.imprint","IMPRINT",EDGE,{"disambiguationData":[TD([[subQ29,-1.0]])],"derivedFrom":subQ2});var subQ31=makeQuery(id+"F3.imprint","IMPRINT",VERTEX,{"disambiguationData":[OD(2.0)],"derivedFrom":subQ2});var subQ32=makeQuery(id+"F3.imprint","IMPRINT",EDGE,{"disambiguationData":[TD([[subQ31,-1.0]])],"derivedFrom":subQ2});var subQ33=makeQuery(id+"F3.imprint","IMPRINT",VERTEX,{"disambiguationData":[OD(1.0)],"derivedFrom":subQ2});var subQ34=makeQuery(id+"F3.imprint","IMPRINT",EDGE,{"disambiguationData":[TD([[subQ33,-1.0]])],"derivedFrom":subQ2});var subQ35=makeQuery(id+"F3.imprint","IMPRINT",VERTEX,{"disambiguationData":[OD(0.0)],"derivedFrom":subQ2});var subQ36=makeQuery(id+"F3.imprint","IMPRINT",EDGE,{"disambiguationData":[TD([[subQ35,-1.0]])],"derivedFrom":subQ2});var subQ38=makeQuery(id+"F3.imprint","IMPRINT",EDGE,{"disambiguationData":[TD([[subQ35,1.0]])],"derivedFrom":subQ2});Q25=makeQuery(id+"F6.boolean.opBoolean","SPLIT",EDGE,{"disambiguationData":[TD([makeQuery(id+"F6.opExtrude","SWEPT_FACE",FACE,{"disambiguationData":[OSD([subQ4])]})])],"derivedFrom":makeQuery(id+"F4.opExtrude","CAP_EDGE",EDGE,{"disambiguationData":[OSD([subQ2]),TDD([subQ38,subQ36,subQ34,subQ32,subQ30,subQ28,subQ26,subQ24,subQ22,subQ20,subQ18,subQ16,subQ14,subQ12])],"isStart":false})});}
            var Q26;
            Q26=makeQuery(id+"F6.opExtrude","CAP_EDGE",EDGE,{"disambiguationData":[OSD([sQuery(id+"F5.wireOp",EDGE,"E50.5.0.0")])],"isStart":false});
            var Q27;
            Q27=makeQuery(id+"F6.opExtrude","CAP_EDGE",EDGE,{"disambiguationData":[OSD([sQuery(id+"F5.wireOp",EDGE,"E50.4.0.0")])],"isStart":false});
            var Q28;
            {var subQ1=sQuery(id+"F3.wireOp",EDGE,"E7");var subQ8=sQuery(id+"F5.wireOp",EDGE,"E50.3.0.0");var subQ9=sQuery(id+"F3.wireOp",EDGE,"E6.0.2");var subQ11=makeQuery(id+"F3.imprint","IMPRINT",EDGE,{"disambiguationData":[TD([[makeQuery(id+"F3.imprint","INTERSECT",VERTEX,{"derivedFrom":[subQ9,subQ1]}),1.0]])],"derivedFrom":subQ1});var subQ12=makeQuery(id+"F3.imprint","IMPRINT",VERTEX,{"disambiguationData":[OD(11.0)],"derivedFrom":subQ1});var subQ13=makeQuery(id+"F3.imprint","IMPRINT",EDGE,{"disambiguationData":[TD([[subQ12,-1.0]])],"derivedFrom":subQ1});var subQ14=makeQuery(id+"F3.imprint","IMPRINT",VERTEX,{"disambiguationData":[OD(10.0)],"derivedFrom":subQ1});var subQ15=makeQuery(id+"F3.imprint","IMPRINT",EDGE,{"disambiguationData":[TD([[subQ14,-1.0]])],"derivedFrom":subQ1});var subQ16=makeQuery(id+"F3.imprint","IMPRINT",VERTEX,{"disambiguationData":[OD(9.0)],"derivedFrom":subQ1});var subQ17=makeQuery(id+"F3.imprint","IMPRINT",EDGE,{"disambiguationData":[TD([[subQ16,-1.0]])],"derivedFrom":subQ1});var subQ18=makeQuery(id+"F3.imprint","IMPRINT",VERTEX,{"disambiguationData":[OD(8.0)],"derivedFrom":subQ1});var subQ19=makeQuery(id+"F3.imprint","IMPRINT",EDGE,{"disambiguationData":[TD([[subQ18,-1.0]])],"derivedFrom":subQ1});var subQ20=makeQuery(id+"F3.imprint","IMPRINT",VERTEX,{"disambiguationData":[OD(7.0)],"derivedFrom":subQ1});var subQ21=makeQuery(id+"F3.imprint","IMPRINT",EDGE,{"disambiguationData":[TD([[subQ20,-1.0]])],"derivedFrom":subQ1});var subQ22=makeQuery(id+"F3.imprint","IMPRINT",VERTEX,{"disambiguationData":[OD(6.0)],"derivedFrom":subQ1});var subQ23=makeQuery(id+"F3.imprint","IMPRINT",EDGE,{"disambiguationData":[TD([[subQ22,-1.0]])],"derivedFrom":subQ1});var subQ24=makeQuery(id+"F3.imprint","IMPRINT",VERTEX,{"disambiguationData":[OD(5.0)],"derivedFrom":subQ1});var subQ25=makeQuery(id+"F3.imprint","IMPRINT",EDGE,{"disambiguationData":[TD([[subQ24,-1.0]])],"derivedFrom":subQ1});var subQ26=makeQuery(id+"F3.imprint","IMPRINT",VERTEX,{"disambiguationData":[OD(4.0)],"derivedFrom":subQ1});var subQ27=makeQuery(id+"F3.imprint","IMPRINT",EDGE,{"disambiguationData":[TD([[subQ26,-1.0]])],"derivedFrom":subQ1});var subQ28=makeQuery(id+"F3.imprint","IMPRINT",VERTEX,{"disambiguationData":[OD(3.0)],"derivedFrom":subQ1});var subQ29=makeQuery(id+"F3.imprint","IMPRINT",EDGE,{"disambiguationData":[TD([[subQ28,-1.0]])],"derivedFrom":subQ1});var subQ30=makeQuery(id+"F3.imprint","IMPRINT",VERTEX,{"disambiguationData":[OD(2.0)],"derivedFrom":subQ1});var subQ31=makeQuery(id+"F3.imprint","IMPRINT",EDGE,{"disambiguationData":[TD([[subQ30,-1.0]])],"derivedFrom":subQ1});var subQ32=makeQuery(id+"F3.imprint","IMPRINT",VERTEX,{"disambiguationData":[OD(1.0)],"derivedFrom":subQ1});var subQ33=makeQuery(id+"F3.imprint","IMPRINT",EDGE,{"disambiguationData":[TD([[subQ32,-1.0]])],"derivedFrom":subQ1});var subQ34=makeQuery(id+"F3.imprint","IMPRINT",VERTEX,{"disambiguationData":[OD(0.0)],"derivedFrom":subQ1});var subQ35=makeQuery(id+"F3.imprint","IMPRINT",EDGE,{"disambiguationData":[TD([[subQ34,-1.0]])],"derivedFrom":subQ1});var subQ38=makeQuery(id+"F3.imprint","IMPRINT",EDGE,{"disambiguationData":[TD([[subQ34,1.0]])],"derivedFrom":subQ1});Q28=makeQuery(id+"F6.boolean.opBoolean","SPLIT",EDGE,{"disambiguationData":[TD([makeQuery(id+"F6.opExtrude","SWEPT_FACE",FACE,{"disambiguationData":[OSD([subQ8])]})])],"derivedFrom":makeQuery(id+"F4.opExtrude","CAP_EDGE",EDGE,{"disambiguationData":[OSD([subQ1]),TDD([subQ38,subQ35,subQ33,subQ31,subQ29,subQ27,subQ25,subQ23,subQ21,subQ19,subQ17,subQ15,subQ13,subQ11])],"isStart":false})});}
            var Q29;
            Q29=makeQuery(id+"F6.opExtrude","CAP_EDGE",EDGE,{"disambiguationData":[OSD([sQuery(id+"F5.wireOp",EDGE,"E50.3.0.0")])],"isStart":false});
            var Q30;
            Q30=makeQuery(id+"F6.opExtrude","CAP_EDGE",EDGE,{"disambiguationData":[OSD([sQuery(id+"F5.wireOp",EDGE,"E50.2.0.0")])],"isStart":false});
            var Q31;
            {var subQ0=sQuery(id+"F3.wireOp",EDGE,"E7");var subQ8=sQuery(id+"F5.wireOp",EDGE,"E50.1.0.0");var subQ9=sQuery(id+"F3.wireOp",EDGE,"E6.0.2");var subQ11=makeQuery(id+"F3.imprint","IMPRINT",EDGE,{"disambiguationData":[TD([[makeQuery(id+"F3.imprint","INTERSECT",VERTEX,{"derivedFrom":[subQ9,subQ0]}),1.0]])],"derivedFrom":subQ0});var subQ12=makeQuery(id+"F3.imprint","IMPRINT",VERTEX,{"disambiguationData":[OD(11.0)],"derivedFrom":subQ0});var subQ13=makeQuery(id+"F3.imprint","IMPRINT",EDGE,{"disambiguationData":[TD([[subQ12,-1.0]])],"derivedFrom":subQ0});var subQ14=makeQuery(id+"F3.imprint","IMPRINT",VERTEX,{"disambiguationData":[OD(10.0)],"derivedFrom":subQ0});var subQ15=makeQuery(id+"F3.imprint","IMPRINT",EDGE,{"disambiguationData":[TD([[subQ14,-1.0]])],"derivedFrom":subQ0});var subQ16=makeQuery(id+"F3.imprint","IMPRINT",VERTEX,{"disambiguationData":[OD(9.0)],"derivedFrom":subQ0});var subQ17=makeQuery(id+"F3.imprint","IMPRINT",EDGE,{"disambiguationData":[TD([[subQ16,-1.0]])],"derivedFrom":subQ0});var subQ18=makeQuery(id+"F3.imprint","IMPRINT",VERTEX,{"disambiguationData":[OD(8.0)],"derivedFrom":subQ0});var subQ19=makeQuery(id+"F3.imprint","IMPRINT",EDGE,{"disambiguationData":[TD([[subQ18,-1.0]])],"derivedFrom":subQ0});var subQ20=makeQuery(id+"F3.imprint","IMPRINT",VERTEX,{"disambiguationData":[OD(7.0)],"derivedFrom":subQ0});var subQ21=makeQuery(id+"F3.imprint","IMPRINT",EDGE,{"disambiguationData":[TD([[subQ20,-1.0]])],"derivedFrom":subQ0});var subQ22=makeQuery(id+"F3.imprint","IMPRINT",VERTEX,{"disambiguationData":[OD(6.0)],"derivedFrom":subQ0});var subQ23=makeQuery(id+"F3.imprint","IMPRINT",EDGE,{"disambiguationData":[TD([[subQ22,-1.0]])],"derivedFrom":subQ0});var subQ24=makeQuery(id+"F3.imprint","IMPRINT",VERTEX,{"disambiguationData":[OD(5.0)],"derivedFrom":subQ0});var subQ25=makeQuery(id+"F3.imprint","IMPRINT",EDGE,{"disambiguationData":[TD([[subQ24,-1.0]])],"derivedFrom":subQ0});var subQ26=makeQuery(id+"F3.imprint","IMPRINT",VERTEX,{"disambiguationData":[OD(4.0)],"derivedFrom":subQ0});var subQ27=makeQuery(id+"F3.imprint","IMPRINT",EDGE,{"disambiguationData":[TD([[subQ26,-1.0]])],"derivedFrom":subQ0});var subQ28=makeQuery(id+"F3.imprint","IMPRINT",VERTEX,{"disambiguationData":[OD(3.0)],"derivedFrom":subQ0});var subQ29=makeQuery(id+"F3.imprint","IMPRINT",EDGE,{"disambiguationData":[TD([[subQ28,-1.0]])],"derivedFrom":subQ0});var subQ30=makeQuery(id+"F3.imprint","IMPRINT",VERTEX,{"disambiguationData":[OD(2.0)],"derivedFrom":subQ0});var subQ31=makeQuery(id+"F3.imprint","IMPRINT",EDGE,{"disambiguationData":[TD([[subQ30,-1.0]])],"derivedFrom":subQ0});var subQ32=makeQuery(id+"F3.imprint","IMPRINT",VERTEX,{"disambiguationData":[OD(1.0)],"derivedFrom":subQ0});var subQ33=makeQuery(id+"F3.imprint","IMPRINT",EDGE,{"disambiguationData":[TD([[subQ32,-1.0]])],"derivedFrom":subQ0});var subQ34=makeQuery(id+"F3.imprint","IMPRINT",VERTEX,{"disambiguationData":[OD(0.0)],"derivedFrom":subQ0});var subQ35=makeQuery(id+"F3.imprint","IMPRINT",EDGE,{"disambiguationData":[TD([[subQ34,-1.0]])],"derivedFrom":subQ0});var subQ38=makeQuery(id+"F3.imprint","IMPRINT",EDGE,{"disambiguationData":[TD([[subQ34,1.0]])],"derivedFrom":subQ0});Q31=makeQuery(id+"F6.boolean.opBoolean","SPLIT",EDGE,{"disambiguationData":[TD([makeQuery(id+"F6.opExtrude","SWEPT_FACE",FACE,{"disambiguationData":[OSD([subQ8])]})])],"derivedFrom":makeQuery(id+"F4.opExtrude","CAP_EDGE",EDGE,{"disambiguationData":[OSD([subQ0]),TDD([subQ38,subQ35,subQ33,subQ31,subQ29,subQ27,subQ25,subQ23,subQ21,subQ19,subQ17,subQ15,subQ13,subQ11])],"isStart":false})});}
            var Q32;
            Q32=makeQuery(id+"F6.opExtrude","CAP_EDGE",EDGE,{"disambiguationData":[OSD([sQuery(id+"F5.wireOp",EDGE,"E50.1.0.0")])],"isStart":false});
            var Q33;
            Q33=makeQuery(id+"F4.opExtrude","CAP_EDGE",EDGE,{"disambiguationData":[OSD([sQuery(id+"F3.wireOp",EDGE,"E10.6.0.0")])],"isStart":false});
            var Q34;
            {var subQ0=sQuery(id+"F3.wireOp",EDGE,"E7");Q34=makeQuery(id+"F4.opExtrude","CAP_EDGE",EDGE,{"disambiguationData":[OSD([subQ0]),TDD([makeQuery(id+"F3.imprint","IMPRINT",EDGE,{"disambiguationData":[TD([[makeQuery(id+"F3.imprint","INTERSECT",VERTEX,{"derivedFrom":[subQ0,sQuery(id+"F3.wireOp",EDGE,"E10.5.0.0")]}),1.0]])],"derivedFrom":subQ0})])],"isStart":false});}
            var Q35;
            Q35=makeQuery(id+"F4.opExtrude","CAP_EDGE",EDGE,{"disambiguationData":[OSD([sQuery(id+"F3.wireOp",EDGE,"E10.5.0.0")])],"isStart":false});
            var Q36;
            Q36=makeQuery(id+"F4.opExtrude","CAP_EDGE",EDGE,{"disambiguationData":[OSD([sQuery(id+"F3.wireOp",EDGE,"E10.4.0.0")])],"isStart":false});
            var Q37;
            {var subQ0=sQuery(id+"F3.wireOp",EDGE,"E7");Q37=makeQuery(id+"F4.opExtrude","CAP_EDGE",EDGE,{"disambiguationData":[OSD([subQ0]),TDD([makeQuery(id+"F3.imprint","IMPRINT",EDGE,{"disambiguationData":[TD([[makeQuery(id+"F3.imprint","INTERSECT",VERTEX,{"derivedFrom":[subQ0,sQuery(id+"F3.wireOp",EDGE,"E10.3.0.0")]}),1.0]])],"derivedFrom":subQ0})])],"isStart":false});}
            var Q38;
            Q38=makeQuery(id+"F4.opExtrude","CAP_EDGE",EDGE,{"disambiguationData":[OSD([sQuery(id+"F3.wireOp",EDGE,"E10.3.0.0")])],"isStart":false});
            var Q39;
            Q39=makeQuery(id+"F4.opExtrude","CAP_EDGE",EDGE,{"disambiguationData":[OSD([sQuery(id+"F3.wireOp",EDGE,"E10.2.0.0")])],"isStart":false});
            var Q40;
            {var subQ0=sQuery(id+"F3.wireOp",EDGE,"E7");Q40=makeQuery(id+"F4.opExtrude","CAP_EDGE",EDGE,{"disambiguationData":[OSD([subQ0]),TDD([makeQuery(id+"F3.imprint","IMPRINT",EDGE,{"disambiguationData":[TD([[makeQuery(id+"F3.imprint","INTERSECT",VERTEX,{"derivedFrom":[subQ0,sQuery(id+"F3.wireOp",EDGE,"E10.1.0.0")]}),1.0]])],"derivedFrom":subQ0})])],"isStart":false});}
            var Q41;
            Q41=makeQuery(id+"F4.opExtrude","CAP_EDGE",EDGE,{"disambiguationData":[OSD([sQuery(id+"F3.wireOp",EDGE,"E10.1.0.0")])],"isStart":false});
            var Q42;
            {var subQ8=sQuery(id+"F5.wireOp",EDGE,"E49");var subQ9=sQuery(id+"F3.wireOp",EDGE,"E9");Q42=makeQuery(id+"F6.boolean.opBoolean","SPLIT",EDGE,{"disambiguationData":[TD([makeQuery(id+"F4.opExtrude","SWEPT_FACE",FACE,{"disambiguationData":[OSD([subQ9])]})])],"derivedFrom":makeQuery(id+"F6.opExtrude","CAP_EDGE",EDGE,{"disambiguationData":[OSD([subQ8])],"isStart":false})});}
            var Q43;
            Q43=makeQuery(id+"F4.opExtrude","CAP_EDGE",EDGE,{"disambiguationData":[OSD([sQuery(id+"F3.wireOp",EDGE,"E9")])],"isStart":false});
            var Q44;
            Q44=makeQuery(id+"F4.opExtrude","CAP_EDGE",EDGE,{"disambiguationData":[OSD([sQuery(id+"F3.wireOp",EDGE,"E11.1.0.0")])],"isStart":false});
            var Q45;
            Q45=makeQuery(id+"F4.opExtrude","CAP_EDGE",EDGE,{"disambiguationData":[OSD([sQuery(id+"F3.wireOp",EDGE,"E11.2.0.0")])],"isStart":false});
            var Q46;
            {var subQ0=sQuery(id+"F5.wireOp",EDGE,"E49");var subQ8=sQuery(id+"F3.wireOp",EDGE,"E11.2.0.0");Q46=makeQuery(id+"F6.boolean.opBoolean","SPLIT",EDGE,{"disambiguationData":[TD([makeQuery(id+"F4.opExtrude","SWEPT_FACE",FACE,{"disambiguationData":[OSD([subQ8])]})])],"derivedFrom":makeQuery(id+"F6.opExtrude","CAP_EDGE",EDGE,{"disambiguationData":[OSD([subQ0])],"isStart":false})});}
            var Q47;
            Q47=makeQuery(id+"F4.opExtrude","CAP_EDGE",EDGE,{"disambiguationData":[OSD([sQuery(id+"F3.wireOp",EDGE,"E11.3.0.0")])],"isStart":false});
            var Q48;
            Q48=makeQuery(id+"F4.opExtrude","CAP_EDGE",EDGE,{"disambiguationData":[OSD([sQuery(id+"F3.wireOp",EDGE,"E11.4.0.0")])],"isStart":false});
            var Q49;
            {var subQ7=sQuery(id+"F5.wireOp",EDGE,"E49");var subQ11=sQuery(id+"F3.wireOp",EDGE,"E11.4.0.0");Q49=makeQuery(id+"F6.boolean.opBoolean","SPLIT",EDGE,{"disambiguationData":[TD([makeQuery(id+"F4.opExtrude","SWEPT_FACE",FACE,{"disambiguationData":[OSD([subQ11])]})])],"derivedFrom":makeQuery(id+"F6.opExtrude","CAP_EDGE",EDGE,{"disambiguationData":[OSD([subQ7])],"isStart":false})});}
            var Q50;
            Q50=makeQuery(id+"F4.opExtrude","CAP_EDGE",EDGE,{"disambiguationData":[OSD([sQuery(id+"F3.wireOp",EDGE,"E11.5.0.0")])],"isStart":false});
            var Q51;
            Q51=makeQuery(id+"F4.opExtrude","CAP_EDGE",EDGE,{"disambiguationData":[OSD([sQuery(id+"F3.wireOp",EDGE,"E11.6.0.0")])],"isStart":false});
            var Q52;
            {var subQ6=sQuery(id+"F0.wireOp",EDGE,"E0");var subQ7=sQuery(id+"F5.wireOp",EDGE,"E49");Q52=makeQuery(id+"F6.boolean.opBoolean","SPLIT",EDGE,{"disambiguationData":[TD([makeQuery(id+"F2.opShell","OFFSET_FACE",FACE,{"disambiguationData":[OSD([subQ6])]})])],"derivedFrom":makeQuery(id+"F6.opExtrude","CAP_EDGE",EDGE,{"disambiguationData":[OSD([subQ7])],"isStart":false})});}
            chamfer(context, id + "F7", {"entities" : qUnion([Q0, Q1, Q2, Q3, Q4, Q5, Q6, Q7, Q8, Q9, Q10, Q11, Q12, Q13, Q14, Q15, Q16, Q17, Q18, Q19, Q20, Q21, Q22, Q23, Q24, Q25, Q26, Q27, Q28, Q29, Q30, Q31, Q32, Q33, Q34, Q35, Q36, Q37, Q38, Q39, Q40, Q41, Q42, Q43, Q44, Q45, Q46, Q47, Q48, Q49, Q50, Q51, Q52]), "width" : 3.8 * mm, "tangentPropagation" : true});
        }
        {
            var Q0;
            Q0=makeQuery(id+"F1.opExtrude","CAP_FACE",FACE,{"disambiguationData":[OSD([sQuery(id+"F0.wireOp",EDGE,"E0"),sQuery(id+"F0.wireOp",EDGE,"E1"),sQuery(id+"F0.wireOp",EDGE,"E2"),sQuery(id+"F0.wireOp",EDGE,"E3.filletArc"),sQuery(id+"F0.wireOp",EDGE,"E4.filletArc"),sQuery(id+"F0.wireOp",EDGE,"E5.filletArc")])],"isStart":true});
            var sketch = newSketch(context, id + "F8", { "sketchPlane" : qUnion([Q0])});
            skLineSegment(sketch, "E51.0", {"start": v(-104.23, 185.32) * mm, "end": v(-3.12, 10.2) * mm});
            skLineSegment(sketch, "E51.1", {"start": v(3.12, 10.2) * mm, "end": v(104.23, 185.32) * mm});
            skArc(sketch, "E51.2", {"start": v(104.23, 185.32) * mm, "mid": v(104.23, 188.92) * mm, "end": v(101.1, 190.72) * mm});
            skArc(sketch, "E51.3", {"start": v(-3.12, 10.2) * mm, "mid": v(0, 8.4) * mm, "end": v(3.12, 10.2) * mm});
            skLineSegment(sketch, "E51.4", {"start": v(101.1, 190.72) * mm, "end": v(-101.1, 190.72) * mm});
            skArc(sketch, "E51.5", {"start": v(-101.1, 190.72) * mm, "mid": v(-104.23, 188.92) * mm, "end": v(-104.23, 185.32) * mm});
            skSolve(sketch);
        }
        {
            var Q0;
            Q0=makeQuery(id+"F8.imprint","IMPRINT",FACE,{"disambiguationData":[TD([[makeQuery(id+"F8.imprint","IMPRINT",EDGE,{"derivedFrom":sQuery(id+"F8.wireOp",EDGE,"E51.0")}),-1.0]])]});
            var Q1;
            Q1=makeQuery(id+"F1.opExtrude","CAP_FACE",FACE,{"disambiguationData":[OSD([sQuery(id+"F0.wireOp",EDGE,"E0"),sQuery(id+"F0.wireOp",EDGE,"E1"),sQuery(id+"F0.wireOp",EDGE,"E2"),sQuery(id+"F0.wireOp",EDGE,"E3.filletArc"),sQuery(id+"F0.wireOp",EDGE,"E4.filletArc"),sQuery(id+"F0.wireOp",EDGE,"E5.filletArc")])],"isStart":false});
            extrude(context, id + "F9", {"entities" : qUnion([Q0]), "operationType" : NewBodyOperationType.ADD, "endBound" : BoundingType.UP_TO_SURFACE, "oppositeDirection" : true, "endBoundEntityFace" : qUnion([Q1]), "depth" : 25 * mm});
        }
        {
            var Q0;
            {var subQ0=sQuery(id+"F0.wireOp",EDGE,"E5.filletArc");var subQ1=sQuery(id+"F0.wireOp",EDGE,"E4.filletArc");var subQ2=sQuery(id+"F0.wireOp",EDGE,"E3.filletArc");var subQ3=sQuery(id+"F0.wireOp",EDGE,"E2");var subQ4=sQuery(id+"F0.wireOp",EDGE,"E1");var subQ5=sQuery(id+"F0.wireOp",EDGE,"E0");Q0=makeQuery(id+"F9.boolean.opBoolean","MERGE",FACE,{"derivedFrom":[makeQuery(id+"F1.opExtrude","CAP_FACE",FACE,{"disambiguationData":[OSD([subQ5,subQ4,subQ3,subQ2,subQ1,subQ0])],"isStart":true}),makeQuery(id+"F9.opExtrude","CAP_FACE",FACE,{"disambiguationData":[OSD([subQ5,subQ4,subQ3,subQ2,subQ1,subQ0,sQuery(id+"F8.wireOp",EDGE,"E51.0"),sQuery(id+"F8.wireOp",EDGE,"E51.1"),sQuery(id+"F8.wireOp",EDGE,"E51.2"),sQuery(id+"F8.wireOp",EDGE,"E51.3"),sQuery(id+"F8.wireOp",EDGE,"E51.4"),sQuery(id+"F8.wireOp",EDGE,"E51.5")])],"isStart":true})]});}
            var sketch = newSketch(context, id + "F10", { "sketchPlane" : qUnion([Q0])});
            skLineSegment(sketch, "E52", {"start": v(-55.75, 96.56) * mm, "end": v(-73.07, 86.56) * mm});
            skLineSegment(sketch, "E53", {"start": v(-73.07, 86.56) * mm, "end": v(-68.57, 78.77) * mm});
            skLineSegment(sketch, "E54", {"start": v(-68.57, 78.77) * mm, "end": v(-51.25, 88.77) * mm});
            skLineSegment(sketch, "E55", {"start": v(-51.25, 88.77) * mm, "end": v(-60.25, 104.36) * mm});
            skLineSegment(sketch, "E56", {"start": v(-60.25, 104.36) * mm, "end": v(-77.57, 94.36) * mm});
            skLineSegment(sketch, "E57", {"start": v(-73.07, 86.56) * mm, "end": v(-77.57, 94.36) * mm});
            skSolve(sketch);
        }
        {
            var Q0;
            Q0=makeQuery(id+"F1.opExtrude","CAP_EDGE",EDGE,{"disambiguationData":[OSD([sQuery(id+"F0.wireOp",EDGE,"E2")])],"isStart":false});
            chamfer(context, id + "F11", {"entities" : qUnion([Q0]), "width" : 0.6 * mm, "tangentPropagation" : true});
        }
        {
            var Q0;
            Q0=makeQuery(id+"F10.imprint","IMPRINT",FACE,{"disambiguationData":[TD([[makeQuery(id+"F10.imprint","IMPRINT",EDGE,{"derivedFrom":makeQuery(id+"F1.opExtrude","CAP_EDGE",EDGE,{"disambiguationData":[OSD([sQuery(id+"F0.wireOp",EDGE,"E1")])],"isStart":true})}),-1.0]])]});
            var sketch = newSketch(context, id + "F12", { "sketchPlane" : qUnion([Q0])});
            skArc(sketch, "E58.0.0", {"start": v(-5.2, 9) * mm, "mid": v(0, 6) * mm, "end": v(5.2, 9) * mm});
            skLineSegment(sketch, "E58.0.1", {"start": v(5.2, 9) * mm, "end": v(106.3, 184.12) * mm});
            skArc(sketch, "E58.0.2", {"start": v(106.3, 184.12) * mm, "mid": v(106.3, 190.12) * mm, "end": v(101.1, 193.12) * mm});
            skLineSegment(sketch, "E58.0.3", {"start": v(101.1, 193.12) * mm, "end": v(-101.1, 193.12) * mm});
            skArc(sketch, "E58.0.4", {"start": v(-101.1, 193.12) * mm, "mid": v(-106.3, 190.12) * mm, "end": v(-106.3, 184.12) * mm});
            skLineSegment(sketch, "E58.0.5", {"start": v(-106.3, 184.12) * mm, "end": v(-60.25, 104.36) * mm});
            skLineSegment(sketch, "E58.0.6", {"start": v(-60.25, 104.36) * mm, "end": v(-55.75, 96.56) * mm});
            skLineSegment(sketch, "E58.0.7", {"start": v(-55.75, 96.56) * mm, "end": v(-51.25, 88.77) * mm});
            skLineSegment(sketch, "E58.0.8", {"start": v(-51.25, 88.77) * mm, "end": v(-5.2, 9) * mm});
            skLineSegment(sketch, "E59.bottom", {"start": v(-15, 196.12) * mm, "end": v(15, 196.12) * mm});
            skLineSegment(sketch, "E59.top", {"start": v(-15, 190.12) * mm, "end": v(15, 190.12) * mm});
            skLineSegment(sketch, "E59.left", {"start": v(-15, 196.12) * mm, "end": v(-15, 190.12) * mm});
            skLineSegment(sketch, "E59.right", {"start": v(15, 196.12) * mm, "end": v(15, 190.12) * mm});
            skPoint(sketch, "E59.middle", {"position": v(0, 193.12) * mm});
            skSolve(sketch);
        }
        {
            var Q0;
            {var subQ5=sQuery(id+"F12.wireOp",EDGE,"E59.bottom");Q0=makeQuery(id+"F12.imprint","IMPRINT",FACE,{"disambiguationData":[TD([[makeQuery(id+"F12.imprint","IMPRINT",EDGE,{"derivedFrom":subQ5}),-1.0]])]});}
            extrude(context, id + "F13", {"entities" : qUnion([Q0]), "operationType" : NewBodyOperationType.ADD, "oppositeDirection" : true, "depth" : 4 * mm});
        }
        {
            var Q0;
            Q0=makeQuery(id+"F13.opExtrude","CAP_EDGE",EDGE,{"disambiguationData":[OSD([sQuery(id+"F12.wireOp",EDGE,"E59.bottom")])],"isStart":false});
            chamfer(context, id + "F14", {"entities" : qUnion([Q0]), "width" : 3 * mm, "tangentPropagation" : true});
        }
        {
            var Q0;
            {var subQ1=sQuery(id+"F0.wireOp",EDGE,"E4.filletArc");var subQ4=sQuery(id+"F0.wireOp",EDGE,"E1");Q0=makeQuery(id+"F13.boolean.opBoolean","SPLIT",EDGE,{"disambiguationData":[TD([makeQuery(id+"F1.opExtrude","SWEPT_FACE",FACE,{"disambiguationData":[OSD([subQ1])]})])],"derivedFrom":makeQuery(id+"F1.opExtrude","CAP_EDGE",EDGE,{"disambiguationData":[OSD([subQ4])],"isStart":true})});}
            chamfer(context, id + "F15", {"entities" : qUnion([Q0]), "width" : 0.6 * mm, "tangentPropagation" : true});
        }
    });
